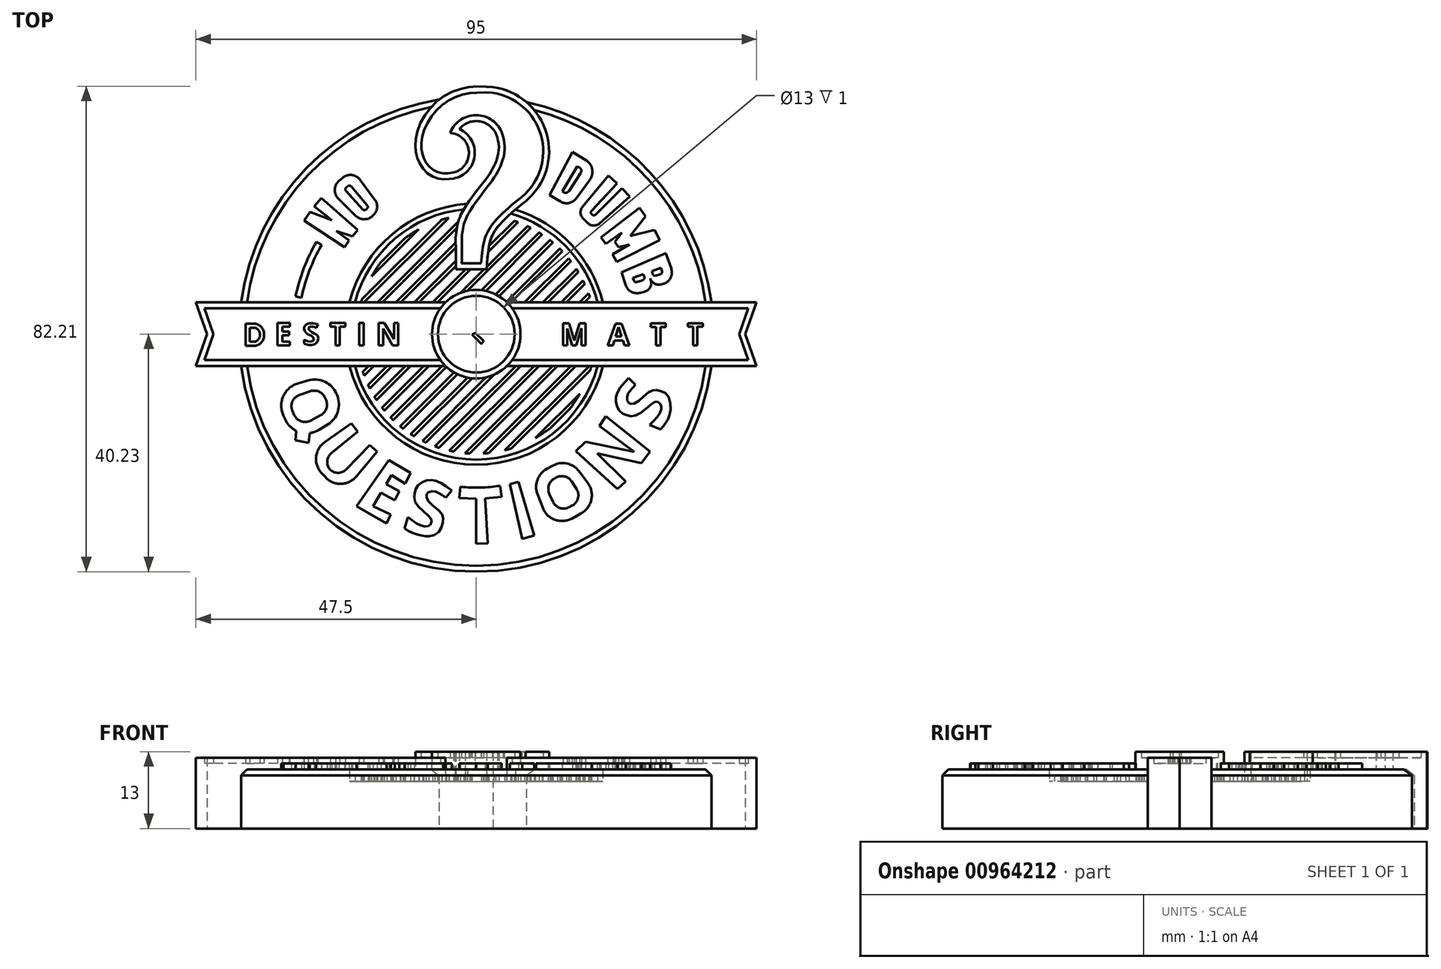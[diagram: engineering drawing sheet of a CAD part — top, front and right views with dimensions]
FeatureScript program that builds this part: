
annotation { "Feature Type Name" : "Feature", "Feature Type Description" : "" }
export const myFeature = defineFeature(function(context is Context, id is Id, definition is map)
    precondition{}
    {
        {
            var Q0;
            Q0=qCreatedBy(makeId("Top.planeOp"),FACE);
            var sketch = newSketch(context, id + "F0", { "sketchPlane" : qUnion([Q0])});
            skCircle(sketch, "E0", {"center": v(0, 0) * mm, "radius": 22.12 * mm});
            skCircle(sketch, "E1", {"center": v(0, 0) * mm, "radius": 40.23 * mm});
            skSolve(sketch);
        }
        {
            var Q0;
            Q0=qCreatedBy(makeId("Top.planeOp"),FACE);
            var sketch = newSketch(context, id + "F1", { "sketchPlane" : qUnion([Q0])});
            skCircle(sketch, "E2", {"center": v(0, 0) * mm, "radius": 22.25 * mm});
            skCircle(sketch, "E3.0", {"center": v(0, 0) * mm, "radius": 21.25 * mm});
            skCircle(sketch, "E4.0", {"center": v(0, 0) * mm, "radius": 20.25 * mm});
            skLineSegment(sketch, "E5", {"start": v(-14.52, -14.12) * mm, "end": v(14.16, 14.48) * mm});
            skLineSegment(sketch, "E6", {"start": v(-14.08, -14.55) * mm, "end": v(14.58, 14.05) * mm});
            skLineSegment(sketch, "E7.0.1.0", {"start": v(-15.97, -12.45) * mm, "end": v(12.5, 15.93) * mm});
            skLineSegment(sketch, "E7.0.2.0", {"start": v(-17.24, -10.62) * mm, "end": v(10.67, 17.21) * mm});
            skLineSegment(sketch, "E7.0.2.1", {"start": v(-16.9, -11.15) * mm, "end": v(11.18, 16.88) * mm});
            skLineSegment(sketch, "E7.1.7.0", {"start": v(-9.13, -18.07) * mm, "end": v(18.1, 9.08) * mm});
            skLineSegment(sketch, "E7.1.7.1", {"start": v(-8.54, -18.36) * mm, "end": v(18.37, 8.51) * mm});
            skLineSegment(sketch, "E7.1.8.0", {"start": v(-11.1, -16.93) * mm, "end": v(16.97, 11.05) * mm});
            skLineSegment(sketch, "E7.1.8.1", {"start": v(-10.57, -17.27) * mm, "end": v(17.3, 10.54) * mm});
            skLineSegment(sketch, "E7.1.9.0", {"start": v(-12.9, -15.61) * mm, "end": v(15.65, 12.85) * mm});
            skLineSegment(sketch, "E7.1.9.1", {"start": v(-12.4, -16) * mm, "end": v(16.02, 12.38) * mm});
            skLineSegment(sketch, "E8.trimOffspring", {"start": v(12.76, -15.72) * mm, "end": v(15.7, -12.8) * mm});
            skLineSegment(sketch, "E9.trimOffspring", {"start": v(10.02, -17.6) * mm, "end": v(17.57, -10.07) * mm});
            skLineSegment(sketch, "E10.trimOffspring", {"start": v(6.04, -19.33) * mm, "end": v(19.32, -6.07) * mm});
            skLineSegment(sketch, "E11.trimOffspring", {"start": v(4.83, -19.67) * mm, "end": v(19.65, -4.89) * mm});
            skLineSegment(sketch, "E12.trimOffspring", {"start": v(2.11, -20.14) * mm, "end": v(20.14, -2.15) * mm});
            skLineSegment(sketch, "E13.trimOffspring", {"start": v(1.16, -20.22) * mm, "end": v(20.21, -1.22) * mm});
            skLineSegment(sketch, "E14.trimOffspring", {"start": v(-1.9, -20.16) * mm, "end": v(20.17, 1.84) * mm});
            skLineSegment(sketch, "E15.trimOffspring", {"start": v(-1.08, -20.22) * mm, "end": v(20.22, 1.05) * mm});
            skLineSegment(sketch, "E16.trimOffspring", {"start": v(-3.85, -19.88) * mm, "end": v(19.89, 3.82) * mm});
            skLineSegment(sketch, "E17.trimOffspring", {"start": v(-4.58, -19.73) * mm, "end": v(19.74, 4.52) * mm});
            skLineSegment(sketch, "E18.trimOffspring", {"start": v(-6.32, -19.24) * mm, "end": v(19.25, 6.3) * mm});
            skLineSegment(sketch, "E19.trimOffspring", {"start": v(-6.98, -19.01) * mm, "end": v(19.03, 6.92) * mm});
            skLineSegment(sketch, "E20.trimOffspring", {"start": v(-15.58, -12.94) * mm, "end": v(12.97, 15.55) * mm});
            skLineSegment(sketch, "E21.trimOffspring", {"start": v(-18.05, -9.19) * mm, "end": v(9.22, 18.03) * mm});
            skLineSegment(sketch, "E22.trimOffspring", {"start": v(-18.33, -8.6) * mm, "end": v(8.66, 18.3) * mm});
            skLineSegment(sketch, "E23.trimOffspring", {"start": v(-19, -7.03) * mm, "end": v(7.06, 18.98) * mm});
            skLineSegment(sketch, "E24.trimOffspring", {"start": v(-19.22, -6.38) * mm, "end": v(6.44, 19.2) * mm});
            skLineSegment(sketch, "E25.trimOffspring", {"start": v(-19.71, -4.63) * mm, "end": v(4.7, 19.7) * mm});
            skLineSegment(sketch, "E26.trimOffspring", {"start": v(-19.87, -3.92) * mm, "end": v(3.98, 19.86) * mm});
            skLineSegment(sketch, "E27.trimOffspring", {"start": v(-20.15, -1.97) * mm, "end": v(2, 20.15) * mm});
            skLineSegment(sketch, "E28.trimOffspring", {"start": v(-20.22, -1.16) * mm, "end": v(1.22, 20.21) * mm});
            skLineSegment(sketch, "E29.trimOffspring", {"start": v(-20.22, 1.07) * mm, "end": v(-1.04, 20.22) * mm});
            skLineSegment(sketch, "E30.trimOffspring", {"start": v(-20.15, 2.01) * mm, "end": v(-1.95, 20.16) * mm});
            skLineSegment(sketch, "E31.trimOffspring", {"start": v(-19.7, 4.7) * mm, "end": v(-4.67, 19.7) * mm});
            skLineSegment(sketch, "E32.trimOffspring", {"start": v(-19.37, 5.9) * mm, "end": v(-5.83, 19.4) * mm});
            skLineSegment(sketch, "E33.trimOffspring", {"start": v(-17.74, 9.76) * mm, "end": v(-9.73, 17.76) * mm});
            skLineSegment(sketch, "E34.trimOffspring", {"start": v(-16.17, 12.2) * mm, "end": v(-12.15, 16.2) * mm});
            skSolve(sketch);
        }
        {
            var Q0;
            Q0=qCreatedBy(makeId("Top.planeOp"),FACE);
            cPlane(context, id + "F2", {"entities" : qUnion([Q0]), "cplaneType" : CPlaneType.OFFSET, "offset" : 10 * mm, "width" : 150 * mm, "height" : 150 * mm});
        }
        {
            var Q0;
            Q0=qCreatedBy(id+"F2.planeOp",FACE);
            var sketch = newSketch(context, id + "F3", { "sketchPlane" : qUnion([Q0])});
            skPoint(sketch, "E35.middle", {"position": v(0, 0) * mm});
            skArc(sketch, "E36", {"start": v(-17.48, 25.92) * mm, "mid": v(-14.44, 27.73) * mm, "end": v(-11.2, 29.19) * mm});
            skArc(sketch, "E37", {"start": v(-16.88, 25.03) * mm, "mid": v(-13.94, 26.78) * mm, "end": v(-10.82, 28.18) * mm});
            skLineSegment(sketch, "E38", {"start": v(0, 0) * mm, "end": v(-12.02, 31.32) * mm, "construction": true});
            skLineSegment(sketch, "E39", {"start": v(0, 0) * mm, "end": v(-17.92, 26.56) * mm, "construction": true});
            skLineSegment(sketch, "E40", {"start": v(0, 0) * mm, "end": v(-28.9, 16.69) * mm, "construction": true});
            skLineSegment(sketch, "E41", {"start": v(0, 0) * mm, "end": v(-31.67, 6.62) * mm, "construction": true});
            skArc(sketch, "E42", {"start": v(-26.19, 15.12) * mm, "mid": v(-28.25, 10.79) * mm, "end": v(-29.6, 6.18) * mm});
            skLineSegment(sketch, "E43", {"start": v(0, 0) * mm, "end": v(-36.69, 24.25) * mm, "construction": true});
            skLineSegment(sketch, "E44", {"start": v(0, 0) * mm, "end": v(-35.15, 25.88) * mm, "construction": true});
            skLineSegment(sketch, "E45", {"start": v(0, 0) * mm, "end": v(-34.07, 26.87) * mm, "construction": true});
            skLineSegment(sketch, "E46", {"start": v(0, 0) * mm, "end": v(-32.8, 28.77) * mm, "construction": true});
            skLineSegment(sketch, "E47", {"start": v(0, 0) * mm, "end": v(-26.52, 35.2) * mm, "construction": true});
            skLineSegment(sketch, "E48", {"start": v(-26.19, 15.12) * mm, "end": v(-27.08, 15.64) * mm});
            skLineSegment(sketch, "E49", {"start": v(-29.6, 6.18) * mm, "end": v(-30.61, 6.4) * mm});
            skLineSegment(sketch, "E50", {"start": v(-16.88, 25.03) * mm, "end": v(-17.48, 25.92) * mm});
            skLineSegment(sketch, "E51", {"start": v(-10.82, 28.18) * mm, "end": v(-11.2, 29.19) * mm});
            skArc(sketch, "E52", {"start": v(-26.73, 0) * mm, "mid": v(0, 26.73) * mm, "end": v(26.73, 0) * mm, "construction": true});
            skArc(sketch, "E53", {"start": v(-34.93, 0) * mm, "mid": v(0, 34.93) * mm, "end": v(34.93, 0) * mm, "construction": true});
            skLineSegment(sketch, "E54", {"start": v(0, 0) * mm, "end": v(-31.72, 31.17) * mm, "construction": true});
            skLineSegment(sketch, "E55", {"start": v(-22.3, 14.74) * mm, "end": v(-29.14, 19.26) * mm});
            skLineSegment(sketch, "E56", {"start": v(-21.52, 15.85) * mm, "end": v(-28.13, 20.71) * mm});
            skLineSegment(sketch, "E57", {"start": v(-20.98, 16.55) * mm, "end": v(-27.43, 21.64) * mm});
            skLineSegment(sketch, "E58", {"start": v(-20.1, 17.62) * mm, "end": v(-26.26, 23.04) * mm});
            skLineSegment(sketch, "E59", {"start": v(-28.13, 20.71) * mm, "end": v(-20.1, 17.62) * mm, "construction": true});
            skLineSegment(sketch, "E60", {"start": v(-20.98, 16.55) * mm, "end": v(-29.14, 19.26) * mm, "construction": true});
            skLineSegment(sketch, "E61", {"start": v(-19.73, 26.18) * mm, "end": v(-17.2, 22.83) * mm});
            skLineSegment(sketch, "E62", {"start": v(-23.38, 22.98) * mm, "end": v(-20.39, 20.03) * mm});
            skLineSegment(sketch, "E63", {"start": v(-23.3, 25.9) * mm, "end": v(-22.64, 26.48) * mm});
            skLineSegment(sketch, "E64", {"start": v(-17.67, 19.96) * mm, "end": v(-17.48, 20.12) * mm});
            skPoint(sketch, "E65.visualSharp", {"position": v(-21.02, 27.9) * mm});
            skArc(sketch, "E65.filletArc", {"start": v(-19.73, 26.18) * mm, "mid": v(-21.12, 26.97) * mm, "end": v(-22.64, 26.48) * mm});
            skPoint(sketch, "E66.visualSharp", {"position": v(-24.92, 24.49) * mm});
            skArc(sketch, "E66.filletArc", {"start": v(-23.3, 25.9) * mm, "mid": v(-23.98, 24.46) * mm, "end": v(-23.38, 22.98) * mm});
            skPoint(sketch, "E67.visualSharp", {"position": v(-16.08, 21.34) * mm});
            skArc(sketch, "E67.filletArc", {"start": v(-17.48, 20.12) * mm, "mid": v(-16.8, 21.42) * mm, "end": v(-17.2, 22.83) * mm});
            skPoint(sketch, "E68.visualSharp", {"position": v(-19.06, 18.73) * mm});
            skArc(sketch, "E68.filletArc", {"start": v(-20.39, 20.03) * mm, "mid": v(-19.04, 19.46) * mm, "end": v(-17.67, 19.96) * mm});
            skLineSegment(sketch, "E69", {"start": v(-20.98, 16.55) * mm, "end": v(-23.72, 17.46) * mm, "construction": true});
            skLineSegment(sketch, "E70", {"start": v(-20.98, 16.55) * mm, "end": v(-23.72, 17.46) * mm});
            skLineSegment(sketch, "E71", {"start": v(-28.13, 20.71) * mm, "end": v(-24.47, 19.3) * mm});
            skLineSegment(sketch, "E72", {"start": v(-29.14, 19.26) * mm, "end": v(-28.13, 20.71) * mm});
            skLineSegment(sketch, "E73", {"start": v(-27.43, 21.64) * mm, "end": v(-26.26, 23.04) * mm});
            skLineSegment(sketch, "E74", {"start": v(-20.98, 16.55) * mm, "end": v(-20.1, 17.62) * mm});
            skLineSegment(sketch, "E75", {"start": v(-22.3, 14.74) * mm, "end": v(-21.52, 15.85) * mm});
            skLineSegment(sketch, "E76", {"start": v(0, 0) * mm, "end": v(-29.4, 32.26) * mm, "construction": true});
            skLineSegment(sketch, "E77", {"start": v(0, 0) * mm, "end": v(-27.98, 33.07) * mm, "construction": true});
            skArc(sketch, "E78", {"start": v(28.2, 0) * mm, "mid": v(0, 28.2) * mm, "end": v(-28.2, 0) * mm, "construction": true});
            skArc(sketch, "E79", {"start": v(33.2, 0) * mm, "mid": v(0, 33.2) * mm, "end": v(-33.2, 0) * mm, "construction": true});
            skArc(sketch, "E80", {"start": v(30.07, 0) * mm, "mid": v(21.26, 21.26) * mm, "end": v(0, 30.07) * mm, "construction": true});
            skArc(sketch, "E81", {"start": v(31.59, 0) * mm, "mid": v(22.34, 22.34) * mm, "end": v(0, 31.59) * mm, "construction": true});
            skLineSegment(sketch, "E82", {"start": v(-19.26, 21.14) * mm, "end": v(-22.08, 24.23) * mm});
            skLineSegment(sketch, "E83", {"start": v(-22.04, 24.8) * mm, "end": v(-21.74, 25.07) * mm});
            skLineSegment(sketch, "E84", {"start": v(-21.17, 25.02) * mm, "end": v(-18.47, 21.83) * mm});
            skLineSegment(sketch, "E85", {"start": v(-18.51, 21.27) * mm, "end": v(-18.7, 21.1) * mm});
            skPoint(sketch, "E86.visualSharp", {"position": v(-22.36, 24.54) * mm});
            skArc(sketch, "E86.filletArc", {"start": v(-22.04, 24.8) * mm, "mid": v(-22.18, 24.53) * mm, "end": v(-22.08, 24.23) * mm});
            skPoint(sketch, "E87.visualSharp", {"position": v(-21.43, 25.33) * mm});
            skArc(sketch, "E87.filletArc", {"start": v(-21.17, 25.02) * mm, "mid": v(-21.45, 25.16) * mm, "end": v(-21.74, 25.07) * mm});
            skPoint(sketch, "E88.visualSharp", {"position": v(-18.22, 21.53) * mm});
            skArc(sketch, "E88.filletArc", {"start": v(-18.51, 21.27) * mm, "mid": v(-18.38, 21.54) * mm, "end": v(-18.47, 21.83) * mm});
            skPoint(sketch, "E89.visualSharp", {"position": v(-19, 20.85) * mm});
            skArc(sketch, "E89.filletArc", {"start": v(-19.26, 21.14) * mm, "mid": v(-18.98, 21) * mm, "end": v(-18.7, 21.1) * mm});
            skArc(sketch, "E90", {"start": v(-30.61, 6.4) * mm, "mid": v(-29.22, 11.16) * mm, "end": v(-27.08, 15.64) * mm});
            skLineSegment(sketch, "E91", {"start": v(0, 0) * mm, "end": v(19.18, 36.3) * mm, "construction": true});
            skLineSegment(sketch, "E92", {"start": v(0, 0) * mm, "end": v(21.24, 35.29) * mm, "construction": true});
            skLineSegment(sketch, "E93", {"start": v(0, 0) * mm, "end": v(22.48, 34.7) * mm, "construction": true});
            skLineSegment(sketch, "E94", {"start": v(0, 0) * mm, "end": v(24.33, 33.05) * mm, "construction": true});
            skLineSegment(sketch, "E95", {"start": v(0, 0) * mm, "end": v(26.82, 32.17) * mm, "construction": true});
            skLineSegment(sketch, "E96", {"start": v(0, 0) * mm, "end": v(28.64, 30.65) * mm, "construction": true});
            skLineSegment(sketch, "E97", {"start": v(0, 0) * mm, "end": v(30.98, 27.8) * mm, "construction": true});
            skLineSegment(sketch, "E98", {"start": v(0, 0) * mm, "end": v(29.35, 29.4) * mm, "construction": true});
            skLineSegment(sketch, "E99", {"start": v(0, 0) * mm, "end": v(32.72, 25.34) * mm, "construction": true});
            skLineSegment(sketch, "E100", {"start": v(0, 0) * mm, "end": v(38.58, 19.83) * mm, "construction": true});
            skLineSegment(sketch, "E101", {"start": v(0, 0) * mm, "end": v(39.4, 16.78) * mm, "construction": true});
            skLineSegment(sketch, "E102", {"start": v(0, 0) * mm, "end": v(40.92, 14.67) * mm, "construction": true});
            skLineSegment(sketch, "E103", {"start": v(0, 0) * mm, "end": v(41.16, 13.39) * mm, "construction": true});
            skLineSegment(sketch, "E104", {"start": v(0, 0) * mm, "end": v(42.33, 11.4) * mm, "construction": true});
            skLineSegment(sketch, "E105", {"start": v(0, 0) * mm, "end": v(41.86, 10.57) * mm, "construction": true});
            skLineSegment(sketch, "E106", {"start": v(0, 0) * mm, "end": v(34.36, 23.93) * mm, "construction": true});
            skLineSegment(sketch, "E107", {"start": v(0, 0) * mm, "end": v(37.3, 21.82) * mm, "construction": true});
            skLineSegment(sketch, "E108", {"start": v(0, 0) * mm, "end": v(35.65, 22.76) * mm, "construction": true});
            skLineSegment(sketch, "E109", {"start": v(0, 0) * mm, "end": v(34.66, 23.09) * mm, "construction": true});
            skLineSegment(sketch, "E110.MirrorCS", {"start": v(0, 0) * mm, "end": v(35.53, 21.73) * mm, "construction": true});
            skLineSegment(sketch, "E111", {"start": v(16.32, 30.89) * mm, "end": v(18.6, 29.46) * mm});
            skLineSegment(sketch, "E112", {"start": v(19.23, 26.12) * mm, "end": v(16.93, 23) * mm});
            skLineSegment(sketch, "E113", {"start": v(14.28, 22.46) * mm, "end": v(12.45, 23.57) * mm});
            skLineSegment(sketch, "E114", {"start": v(12.45, 23.57) * mm, "end": v(16.32, 30.89) * mm});
            skLineSegment(sketch, "E115", {"start": v(17.12, 28.44) * mm, "end": v(17.5, 28.22) * mm});
            skLineSegment(sketch, "E116", {"start": v(17.7, 27.32) * mm, "end": v(15.71, 24.25) * mm});
            skLineSegment(sketch, "E117", {"start": v(14.75, 24.05) * mm, "end": v(14.55, 24.17) * mm});
            skLineSegment(sketch, "E118", {"start": v(14.55, 24.17) * mm, "end": v(17.12, 28.44) * mm});
            skPoint(sketch, "E119.visualSharp", {"position": v(20.71, 28.13) * mm});
            skArc(sketch, "E119.filletArc", {"start": v(19.23, 26.12) * mm, "mid": v(19.64, 27.93) * mm, "end": v(18.6, 29.46) * mm});
            skPoint(sketch, "E120.visualSharp", {"position": v(15.85, 21.52) * mm});
            skArc(sketch, "E120.filletArc", {"start": v(14.28, 22.46) * mm, "mid": v(15.7, 22.21) * mm, "end": v(16.93, 23) * mm});
            skPoint(sketch, "E121.visualSharp", {"position": v(18.06, 27.88) * mm});
            skArc(sketch, "E121.filletArc", {"start": v(17.7, 27.32) * mm, "mid": v(17.79, 27.82) * mm, "end": v(17.5, 28.22) * mm});
            skPoint(sketch, "E122.visualSharp", {"position": v(15.33, 23.67) * mm});
            skArc(sketch, "E122.filletArc", {"start": v(14.75, 24.05) * mm, "mid": v(15.27, 23.95) * mm, "end": v(15.71, 24.25) * mm});
            skLineSegment(sketch, "E123", {"start": v(23.85, 25.52) * mm, "end": v(22.4, 26.88) * mm});
            skLineSegment(sketch, "E124", {"start": v(22.4, 26.88) * mm, "end": v(18, 21.6) * mm});
            skLineSegment(sketch, "E125", {"start": v(18.12, 19.56) * mm, "end": v(18.89, 18.82) * mm});
            skLineSegment(sketch, "E126", {"start": v(20.93, 18.78) * mm, "end": v(26, 23.33) * mm});
            skLineSegment(sketch, "E127", {"start": v(26, 23.33) * mm, "end": v(24.68, 24.72) * mm});
            skLineSegment(sketch, "E128", {"start": v(24.68, 24.72) * mm, "end": v(20.2, 20.24) * mm});
            skLineSegment(sketch, "E129", {"start": v(19.64, 20.24) * mm, "end": v(19.54, 20.34) * mm});
            skLineSegment(sketch, "E130", {"start": v(19.53, 20.9) * mm, "end": v(23.85, 25.52) * mm});
            skPoint(sketch, "E131.visualSharp", {"position": v(19.9, 17.85) * mm});
            skArc(sketch, "E131.filletArc", {"start": v(18.89, 18.82) * mm, "mid": v(19.9, 18.4) * mm, "end": v(20.93, 18.78) * mm});
            skPoint(sketch, "E132.visualSharp", {"position": v(17.11, 20.53) * mm});
            skArc(sketch, "E132.filletArc", {"start": v(18, 21.6) * mm, "mid": v(17.66, 20.56) * mm, "end": v(18.12, 19.56) * mm});
            skPoint(sketch, "E133.visualSharp", {"position": v(19.26, 20.62) * mm});
            skArc(sketch, "E133.filletArc", {"start": v(19.53, 20.9) * mm, "mid": v(19.42, 20.62) * mm, "end": v(19.54, 20.34) * mm});
            skPoint(sketch, "E134.visualSharp", {"position": v(19.92, 19.96) * mm});
            skArc(sketch, "E134.filletArc", {"start": v(19.64, 20.24) * mm, "mid": v(19.92, 20.12) * mm, "end": v(20.2, 20.24) * mm});
            skArc(sketch, "E135", {"start": v(30.94, 0) * mm, "mid": v(21.88, 21.88) * mm, "end": v(0, 30.94) * mm, "construction": true});
            skLineSegment(sketch, "E136", {"start": v(24.59, 10.47) * mm, "end": v(25.32, 8.3) * mm});
            skLineSegment(sketch, "E137", {"start": v(27.7, 7) * mm, "end": v(28.52, 7.2) * mm});
            skLineSegment(sketch, "E138", {"start": v(31.32, 8.43) * mm, "end": v(31.66, 8.52) * mm});
            skLineSegment(sketch, "E139", {"start": v(33.03, 11.1) * mm, "end": v(32.14, 13.7) * mm});
            skLineSegment(sketch, "E140", {"start": v(32.14, 13.7) * mm, "end": v(24.59, 10.47) * mm});
            skLineSegment(sketch, "E141", {"start": v(0, 0) * mm, "end": v(41.39, 12.16) * mm, "construction": true});
            skLineSegment(sketch, "E142", {"start": v(29.69, 8.72) * mm, "end": v(29.6, 9.05) * mm});
            skPoint(sketch, "E143.visualSharp", {"position": v(25.91, 6.54) * mm});
            skArc(sketch, "E143.filletArc", {"start": v(25.32, 8.3) * mm, "mid": v(26.26, 7.18) * mm, "end": v(27.7, 7) * mm});
            skPoint(sketch, "E144.visualSharp", {"position": v(30, 7.58) * mm});
            skArc(sketch, "E144.filletArc", {"start": v(28.52, 7.2) * mm, "mid": v(29.45, 7.9) * mm, "end": v(29.6, 9.05) * mm});
            skPoint(sketch, "E145.visualSharp", {"position": v(33.73, 9.08) * mm});
            skArc(sketch, "E145.filletArc", {"start": v(31.66, 8.52) * mm, "mid": v(32.9, 9.52) * mm, "end": v(33.03, 11.1) * mm});
            skLineSegment(sketch, "E146", {"start": v(29.48, 9.48) * mm, "end": v(29.69, 8.72) * mm});
            skPoint(sketch, "E147.visualSharp", {"position": v(29.87, 8.04) * mm});
            skArc(sketch, "E147.filletArc", {"start": v(29.48, 9.48) * mm, "mid": v(30.18, 8.58) * mm, "end": v(31.32, 8.43) * mm});
            skLineSegment(sketch, "E148", {"start": v(26.55, 9.52) * mm, "end": v(26.7, 9.1) * mm});
            skLineSegment(sketch, "E149", {"start": v(27.2, 8.84) * mm, "end": v(28.21, 9.18) * mm});
            skLineSegment(sketch, "E150", {"start": v(28.47, 9.68) * mm, "end": v(28.32, 10.15) * mm});
            skLineSegment(sketch, "E151", {"start": v(28.32, 10.15) * mm, "end": v(26.55, 9.52) * mm});
            skLineSegment(sketch, "E152", {"start": v(29.73, 10.66) * mm, "end": v(29.91, 10.14) * mm});
            skLineSegment(sketch, "E153", {"start": v(30.41, 9.9) * mm, "end": v(31.2, 10.14) * mm});
            skLineSegment(sketch, "E154", {"start": v(31.45, 10.65) * mm, "end": v(31.27, 11.21) * mm});
            skLineSegment(sketch, "E155", {"start": v(31.27, 11.21) * mm, "end": v(29.73, 10.66) * mm});
            skPoint(sketch, "E156.visualSharp", {"position": v(26.82, 8.72) * mm});
            skArc(sketch, "E156.filletArc", {"start": v(26.7, 9.1) * mm, "mid": v(26.89, 8.87) * mm, "end": v(27.2, 8.84) * mm});
            skPoint(sketch, "E157.visualSharp", {"position": v(28.6, 9.3) * mm});
            skArc(sketch, "E157.filletArc", {"start": v(28.21, 9.18) * mm, "mid": v(28.45, 9.37) * mm, "end": v(28.47, 9.68) * mm});
            skPoint(sketch, "E158.visualSharp", {"position": v(30.04, 9.77) * mm});
            skArc(sketch, "E158.filletArc", {"start": v(29.91, 10.14) * mm, "mid": v(30.11, 9.91) * mm, "end": v(30.41, 9.9) * mm});
            skPoint(sketch, "E159.visualSharp", {"position": v(31.57, 10.27) * mm});
            skArc(sketch, "E159.filletArc", {"start": v(31.2, 10.14) * mm, "mid": v(31.42, 10.34) * mm, "end": v(31.45, 10.65) * mm});
            skLineSegment(sketch, "E160", {"start": v(21.13, 16.36) * mm, "end": v(21.93, 15.28) * mm});
            skLineSegment(sketch, "E161", {"start": v(21.93, 15.28) * mm, "end": v(24.67, 17.19) * mm});
            skLineSegment(sketch, "E162", {"start": v(24.67, 17.19) * mm, "end": v(23.47, 15.63) * mm});
            skLineSegment(sketch, "E163", {"start": v(23.47, 15.63) * mm, "end": v(24.08, 14.72) * mm});
            skLineSegment(sketch, "E164", {"start": v(24.08, 14.72) * mm, "end": v(25.95, 15.19) * mm});
            skLineSegment(sketch, "E165", {"start": v(25.95, 15.19) * mm, "end": v(23.07, 13.5) * mm});
            skLineSegment(sketch, "E166", {"start": v(23.07, 13.5) * mm, "end": v(23.8, 12.24) * mm});
            skLineSegment(sketch, "E167", {"start": v(23.8, 12.24) * mm, "end": v(31.07, 15.97) * mm});
            skLineSegment(sketch, "E168", {"start": v(31.07, 15.97) * mm, "end": v(30.2, 17.67) * mm});
            skLineSegment(sketch, "E169", {"start": v(30.2, 17.67) * mm, "end": v(26.08, 16.65) * mm});
            skLineSegment(sketch, "E170", {"start": v(26.08, 16.65) * mm, "end": v(28.67, 19.97) * mm});
            skLineSegment(sketch, "E171", {"start": v(28.67, 19.97) * mm, "end": v(27.66, 21.42) * mm});
            skLineSegment(sketch, "E172", {"start": v(27.66, 21.42) * mm, "end": v(21.13, 16.36) * mm});
            skSolve(sketch);
        }
        {
            var Q0;
            Q0=qCreatedBy(id+"F2.planeOp",FACE);
            var sketch = newSketch(context, id + "F4", { "sketchPlane" : qUnion([Q0])});
            skArc(sketch, "E173", {"start": v(-26, 0) * mm, "mid": v(0, -26) * mm, "end": v(26, 0) * mm, "construction": true});
            skArc(sketch, "E174", {"start": v(-35.5, 0) * mm, "mid": v(0, -35.5) * mm, "end": v(35.5, 0) * mm, "construction": true});
            skLineSegment(sketch, "E175", {"start": v(0, 0) * mm, "end": v(-42.38, -11.68) * mm, "construction": true});
            skLineSegment(sketch, "E176", {"start": v(0, 0) * mm, "end": v(-42.12, -14.5) * mm, "construction": true});
            skLineSegment(sketch, "E177", {"start": v(0, 0) * mm, "end": v(-39.57, -20.63) * mm, "construction": true});
            skLineSegment(sketch, "E178", {"start": v(0, 0) * mm, "end": v(-38.55, -23.44) * mm, "construction": true});
            skLineSegment(sketch, "E179", {"start": v(0, 0) * mm, "end": v(-37.55, -24.34) * mm, "construction": true});
            skLineSegment(sketch, "E180", {"start": v(0, 0) * mm, "end": v(-36.48, -25.99) * mm, "construction": true});
            skLineSegment(sketch, "E181", {"start": v(0, 0) * mm, "end": v(-34.37, -28.21) * mm, "construction": true});
            skLineSegment(sketch, "E182", {"start": v(0, 0) * mm, "end": v(-30.39, -31.61) * mm, "construction": true});
            skLineSegment(sketch, "E183", {"start": v(0, 0) * mm, "end": v(-28.05, -33.25) * mm, "construction": true});
            skLineSegment(sketch, "E184", {"start": v(0, 0) * mm, "end": v(-24.41, -35.13) * mm, "construction": true});
            skLineSegment(sketch, "E185", {"start": v(0, 0) * mm, "end": v(-22.3, -37.12) * mm, "construction": true});
            skLineSegment(sketch, "E186", {"start": v(0, 0) * mm, "end": v(-18.67, -39.35) * mm, "construction": true});
            skLineSegment(sketch, "E187", {"start": v(0, 0) * mm, "end": v(-15.5, -40.87) * mm, "construction": true});
            skLineSegment(sketch, "E188", {"start": v(0, 0) * mm, "end": v(-12.8, -41.46) * mm, "construction": true});
            skLineSegment(sketch, "E189", {"start": v(0, 0) * mm, "end": v(-10.11, -42.04) * mm, "construction": true});
            skLineSegment(sketch, "E190", {"start": v(0, 0) * mm, "end": v(-7.42, -42.4) * mm, "construction": true});
            skLineSegment(sketch, "E191", {"start": v(0, 0) * mm, "end": v(-4.37, -42.4) * mm, "construction": true});
            skLineSegment(sketch, "E192", {"start": v(0, 0) * mm, "end": v(2.31, -42.28) * mm, "construction": true});
            skLineSegment(sketch, "E193", {"start": v(0, 0) * mm, "end": v(6.53, -41.7) * mm, "construction": true});
            skLineSegment(sketch, "E194", {"start": v(0, 0) * mm, "end": v(9.34, -41.7) * mm, "construction": true});
            skLineSegment(sketch, "E195", {"start": v(0, 0) * mm, "end": v(11.8, -41.1) * mm, "construction": true});
            skLineSegment(sketch, "E196", {"start": v(0, 0) * mm, "end": v(15.56, -40.64) * mm, "construction": true});
            skLineSegment(sketch, "E197", {"start": v(0, 0) * mm, "end": v(18.13, -39.58) * mm, "construction": true});
            skLineSegment(sketch, "E198", {"start": v(0, 0) * mm, "end": v(23.33, -36) * mm, "construction": true});
            skLineSegment(sketch, "E199", {"start": v(0, 0) * mm, "end": v(26.13, -34.86) * mm, "construction": true});
            skLineSegment(sketch, "E200", {"start": v(0, 0) * mm, "end": v(29.84, -32.78) * mm, "construction": true});
            skLineSegment(sketch, "E201", {"start": v(0, 0) * mm, "end": v(32.46, -31.96) * mm, "construction": true});
            skLineSegment(sketch, "E202", {"start": v(0, 0) * mm, "end": v(34.9, -26) * mm, "construction": true});
            skLineSegment(sketch, "E203", {"start": v(0, 0) * mm, "end": v(35.43, -23.91) * mm, "construction": true});
            skLineSegment(sketch, "E204", {"start": v(0, 0) * mm, "end": v(30.96, -29.01) * mm, "construction": true});
            skLineSegment(sketch, "E205", {"start": v(0, 0) * mm, "end": v(33.65, -26.3) * mm, "construction": true});
            skLineSegment(sketch, "E206", {"start": v(0, 0) * mm, "end": v(39.04, -20.72) * mm, "construction": true});
            skLineSegment(sketch, "E207", {"start": v(0, 0) * mm, "end": v(40.59, -18.27) * mm, "construction": true});
            skLineSegment(sketch, "E208", {"start": v(0, 0) * mm, "end": v(41.17, -15.7) * mm, "construction": true});
            skLineSegment(sketch, "E209", {"start": v(0, 0) * mm, "end": v(42.04, -12.99) * mm, "construction": true});
            skArc(sketch, "E210", {"start": v(-27.88, 0) * mm, "mid": v(0, -27.88) * mm, "end": v(27.88, 0) * mm, "construction": true});
            skArc(sketch, "E211", {"start": v(-33.84, 0) * mm, "mid": v(0, -33.84) * mm, "end": v(33.84, 0) * mm, "construction": true});
            skArc(sketch, "E212", {"start": v(-33.37, 0) * mm, "mid": v(0, -33.37) * mm, "end": v(33.37, 0) * mm, "construction": true});
            skArc(sketch, "E213", {"start": v(-31.33, 0) * mm, "mid": v(0, -31.33) * mm, "end": v(31.33, 0) * mm, "construction": true});
            skArc(sketch, "E214", {"start": v(-29.65, 0) * mm, "mid": v(0, -29.65) * mm, "end": v(29.65, 0) * mm, "construction": true});
            skArc(sketch, "E215", {"start": v(-35, 0) * mm, "mid": v(0, -35) * mm, "end": v(35, 0) * mm, "construction": true});
            skArc(sketch, "E216", {"start": v(-26.65, 0) * mm, "mid": v(0, -26.65) * mm, "end": v(26.65, 0) * mm, "construction": true});
            skArc(sketch, "E217", {"start": v(-34.6, 0) * mm, "mid": v(-24.47, -24.47) * mm, "end": v(0, -34.6) * mm, "construction": true});
            skArc(sketch, "E218", {"start": v(-32.7, 0) * mm, "mid": v(-23.13, -23.13) * mm, "end": v(0, -32.7) * mm, "construction": true});
            skLineSegment(sketch, "E219", {"start": v(0, 0) * mm, "end": v(-38.79, -22.77) * mm, "construction": true});
            skLineSegment(sketch, "E220", {"start": v(0, 0) * mm, "end": v(-39.38, -21.72) * mm, "construction": true});
            skLineSegment(sketch, "E221", {"start": v(0, 0) * mm, "end": v(-41.75, -17.7) * mm, "construction": true});
            skLineSegment(sketch, "E222", {"start": v(-28.4, -18.4) * mm, "end": v(-28.2, -16.56) * mm});
            skLineSegment(sketch, "E223", {"start": v(-28.4, -18.4) * mm, "end": v(-30.61, -17.97) * mm});
            skLineSegment(sketch, "E224", {"start": v(-32.68, -13.86) * mm, "end": v(-32.3, -14.62) * mm});
            skLineSegment(sketch, "E225", {"start": v(-26.66, -16.2) * mm, "end": v(-25.19, -15.32) * mm});
            skLineSegment(sketch, "E226", {"start": v(-23.6, -10.31) * mm, "end": v(-23.69, -10.1) * mm});
            skLineSegment(sketch, "E227", {"start": v(-28.42, -7.83) * mm, "end": v(-30.1, -8.3) * mm});
            skLineSegment(sketch, "E228", {"start": v(-32.82, -13.47) * mm, "end": v(-32.68, -13.86) * mm});
            skPoint(sketch, "E229.visualSharp", {"position": v(-25.07, -6.9) * mm});
            skArc(sketch, "E229.filletArc", {"start": v(-23.69, -10.1) * mm, "mid": v(-25.63, -8.08) * mm, "end": v(-28.42, -7.83) * mm});
            skPoint(sketch, "E230.visualSharp", {"position": v(-22.22, -13.5) * mm});
            skArc(sketch, "E230.filletArc", {"start": v(-25.19, -15.32) * mm, "mid": v(-23.46, -13.11) * mm, "end": v(-23.6, -10.31) * mm});
            skPoint(sketch, "E231.visualSharp", {"position": v(-30.33, -18.44) * mm});
            skArc(sketch, "E231.filletArc", {"start": v(-32.3, -14.62) * mm, "mid": v(-29.82, -16.64) * mm, "end": v(-26.66, -16.2) * mm});
            skPoint(sketch, "E232.visualSharp", {"position": v(-34.22, -9.43) * mm});
            skArc(sketch, "E232.filletArc", {"start": v(-30.1, -8.3) * mm, "mid": v(-32.58, -10.3) * mm, "end": v(-32.82, -13.47) * mm});
            skLineSegment(sketch, "E233", {"start": v(-30.61, -17.97) * mm, "end": v(-30.48, -16.39) * mm});
            skPoint(sketch, "E234.visualSharp", {"position": v(-27.58, -4.06) * mm});
            skLineSegment(sketch, "E235", {"start": v(-21.18, -15.08) * mm, "end": v(-25.68, -18.3) * mm});
            skLineSegment(sketch, "E236", {"start": v(-26.22, -23.52) * mm, "end": v(-25.58, -24.22) * mm});
            skLineSegment(sketch, "E237", {"start": v(-20.33, -24.1) * mm, "end": v(-16.76, -19.88) * mm});
            skLineSegment(sketch, "E238", {"start": v(-16.76, -19.88) * mm, "end": v(-18.06, -18.78) * mm});
            skLineSegment(sketch, "E239", {"start": v(-18.06, -18.78) * mm, "end": v(-21.98, -22.86) * mm});
            skLineSegment(sketch, "E240", {"start": v(-24.71, -23.03) * mm, "end": v(-24.89, -22.84) * mm});
            skLineSegment(sketch, "E241", {"start": v(-24.51, -20.12) * mm, "end": v(-20.1, -16.5) * mm});
            skLineSegment(sketch, "E242", {"start": v(-20.1, -16.5) * mm, "end": v(-21.18, -15.08) * mm});
            skPoint(sketch, "E243.visualSharp", {"position": v(-28.91, -20.6) * mm});
            skArc(sketch, "E243.filletArc", {"start": v(-25.68, -18.3) * mm, "mid": v(-27.13, -20.78) * mm, "end": v(-26.22, -23.52) * mm});
            skPoint(sketch, "E244.visualSharp", {"position": v(-22.89, -27.14) * mm});
            skArc(sketch, "E244.filletArc", {"start": v(-25.58, -24.22) * mm, "mid": v(-22.93, -25.35) * mm, "end": v(-20.33, -24.1) * mm});
            skPoint(sketch, "E245.visualSharp", {"position": v(-23.45, -24.4) * mm});
            skArc(sketch, "E245.filletArc", {"start": v(-24.89, -22.84) * mm, "mid": v(-23.44, -23.48) * mm, "end": v(-21.98, -22.86) * mm});
            skPoint(sketch, "E246.visualSharp", {"position": v(-26.15, -21.47) * mm});
            skArc(sketch, "E246.filletArc", {"start": v(-24.51, -20.12) * mm, "mid": v(-25.24, -21.53) * mm, "end": v(-24.71, -23.03) * mm});
            skLineSegment(sketch, "E247", {"start": v(-28.12, -9.67) * mm, "end": v(-29.96, -10.3) * mm});
            skLineSegment(sketch, "E248", {"start": v(-31.15, -12.99) * mm, "end": v(-30.86, -13.66) * mm});
            skLineSegment(sketch, "E249", {"start": v(-28.1, -14.64) * mm, "end": v(-26.37, -13.74) * mm});
            skLineSegment(sketch, "E250", {"start": v(-25.45, -11.18) * mm, "end": v(-25.63, -10.77) * mm});
            skPoint(sketch, "E251.visualSharp", {"position": v(-32, -11) * mm});
            skArc(sketch, "E251.filletArc", {"start": v(-29.96, -10.3) * mm, "mid": v(-31.14, -11.39) * mm, "end": v(-31.15, -12.99) * mm});
            skPoint(sketch, "E252.visualSharp", {"position": v(-30, -15.64) * mm});
            skArc(sketch, "E252.filletArc", {"start": v(-30.86, -13.66) * mm, "mid": v(-29.69, -14.76) * mm, "end": v(-28.1, -14.64) * mm});
            skPoint(sketch, "E253.visualSharp", {"position": v(-24.72, -12.89) * mm});
            skArc(sketch, "E253.filletArc", {"start": v(-26.37, -13.74) * mm, "mid": v(-25.4, -12.64) * mm, "end": v(-25.45, -11.18) * mm});
            skPoint(sketch, "E254.visualSharp", {"position": v(-26.36, -9.07) * mm});
            skArc(sketch, "E254.filletArc", {"start": v(-25.63, -10.77) * mm, "mid": v(-26.66, -9.73) * mm, "end": v(-28.12, -9.67) * mm});
            skLineSegment(sketch, "E255", {"start": v(-11.14, -23.5) * mm, "end": v(-14.84, -21.35) * mm});
            skLineSegment(sketch, "E256", {"start": v(-14.84, -21.35) * mm, "end": v(-20.26, -29.15) * mm});
            skLineSegment(sketch, "E257", {"start": v(-20.26, -29.15) * mm, "end": v(-15.22, -32.07) * mm});
            skLineSegment(sketch, "E258", {"start": v(-15.22, -32.07) * mm, "end": v(-14.5, -30.57) * mm});
            skLineSegment(sketch, "E259", {"start": v(-14.5, -30.57) * mm, "end": v(-17.5, -29.14) * mm});
            skLineSegment(sketch, "E260", {"start": v(-15.27, -25.42) * mm, "end": v(-14.36, -23.9) * mm});
            skLineSegment(sketch, "E261", {"start": v(-14.36, -23.9) * mm, "end": v(-12, -25.3) * mm});
            skLineSegment(sketch, "E262", {"start": v(-12, -25.3) * mm, "end": v(-11.14, -23.5) * mm});
            skLineSegment(sketch, "E263", {"start": v(0, 0) * mm, "end": v(-19.16, -39.14) * mm, "construction": true});
            skLineSegment(sketch, "E264", {"start": v(-17.5, -29.14) * mm, "end": v(-16.13, -26.85) * mm});
            skLineSegment(sketch, "E265", {"start": v(-16.13, -26.85) * mm, "end": v(-13.77, -28.13) * mm});
            skLineSegment(sketch, "E266", {"start": v(-13.77, -28.13) * mm, "end": v(-13.04, -26.63) * mm});
            skLineSegment(sketch, "E267", {"start": v(-13.04, -26.63) * mm, "end": v(-15.27, -25.42) * mm});
            skLineSegment(sketch, "E268", {"start": v(-2.67, -25.86) * mm, "end": v(-2.86, -27.73) * mm});
            skLineSegment(sketch, "E269", {"start": v(-2.86, -27.73) * mm, "end": v(0, -27.88) * mm});
            skLineSegment(sketch, "E270", {"start": v(0, -27.88) * mm, "end": v(0, -35.5) * mm});
            skLineSegment(sketch, "E271", {"start": v(0, -35.5) * mm, "end": v(1.94, -35.45) * mm});
            skLineSegment(sketch, "E272", {"start": v(1.94, -35.45) * mm, "end": v(1.52, -27.84) * mm});
            skLineSegment(sketch, "E273", {"start": v(1.52, -27.84) * mm, "end": v(4.31, -27.54) * mm});
            skLineSegment(sketch, "E274", {"start": v(4.31, -27.54) * mm, "end": v(4.02, -25.69) * mm});
            skLineSegment(sketch, "E275", {"start": v(5.69, -25.37) * mm, "end": v(7.76, -34.64) * mm});
            skLineSegment(sketch, "E276", {"start": v(7.76, -34.64) * mm, "end": v(9.8, -34.12) * mm});
            skLineSegment(sketch, "E277", {"start": v(9.8, -34.12) * mm, "end": v(7.18, -25) * mm});
            skLineSegment(sketch, "E278", {"start": v(7.18, -25) * mm, "end": v(5.69, -25.37) * mm});
            skArc(sketch, "E279", {"start": v(4.02, -25.69) * mm, "mid": v(0.68, -26) * mm, "end": v(-2.67, -25.86) * mm});
            skLineSegment(sketch, "E280", {"start": v(10.38, -27.13) * mm, "end": v(11.25, -29.4) * mm});
            skLineSegment(sketch, "E281", {"start": v(16.21, -31.2) * mm, "end": v(17.77, -30.35) * mm});
            skLineSegment(sketch, "E282", {"start": v(18.88, -25.18) * mm, "end": v(17.42, -23.24) * mm});
            skLineSegment(sketch, "E283", {"start": v(12.93, -22.27) * mm, "end": v(11.96, -22.81) * mm});
            skLineSegment(sketch, "E284", {"start": v(12.39, -27.04) * mm, "end": v(13, -28.38) * mm});
            skLineSegment(sketch, "E285", {"start": v(16.98, -26.2) * mm, "end": v(16.17, -24.95) * mm});
            skLineSegment(sketch, "E286", {"start": v(13.53, -24.29) * mm, "end": v(13.24, -24.45) * mm});
            skPoint(sketch, "E287.visualSharp", {"position": v(12.7, -33.15) * mm});
            skArc(sketch, "E287.filletArc", {"start": v(11.25, -29.4) * mm, "mid": v(13.32, -31.43) * mm, "end": v(16.21, -31.2) * mm});
            skPoint(sketch, "E288.visualSharp", {"position": v(21.3, -28.4) * mm});
            skArc(sketch, "E288.filletArc", {"start": v(17.77, -30.35) * mm, "mid": v(19.5, -28.02) * mm, "end": v(18.88, -25.18) * mm});
            skPoint(sketch, "E289.visualSharp", {"position": v(15.6, -20.8) * mm});
            skArc(sketch, "E289.filletArc", {"start": v(17.42, -23.24) * mm, "mid": v(15.36, -21.92) * mm, "end": v(12.93, -22.27) * mm});
            skPoint(sketch, "E290.visualSharp", {"position": v(9.3, -24.28) * mm});
            skArc(sketch, "E290.filletArc", {"start": v(11.96, -22.81) * mm, "mid": v(10.36, -24.67) * mm, "end": v(10.38, -27.13) * mm});
            skPoint(sketch, "E291.visualSharp", {"position": v(15.16, -23.4) * mm});
            skArc(sketch, "E291.filletArc", {"start": v(16.17, -24.95) * mm, "mid": v(14.98, -24.1) * mm, "end": v(13.53, -24.29) * mm});
            skPoint(sketch, "E292.visualSharp", {"position": v(11.61, -25.34) * mm});
            skArc(sketch, "E292.filletArc", {"start": v(13.24, -24.45) * mm, "mid": v(12.3, -25.57) * mm, "end": v(12.39, -27.04) * mm});
            skLineSegment(sketch, "E293", {"start": v(17.5, -19.23) * mm, "end": v(23.9, -26.25) * mm});
            skLineSegment(sketch, "E294", {"start": v(23.9, -26.25) * mm, "end": v(25.33, -24.95) * mm});
            skLineSegment(sketch, "E295", {"start": v(25.33, -24.95) * mm, "end": v(19.86, -19.56) * mm});
            skLineSegment(sketch, "E296", {"start": v(27.97, -21.86) * mm, "end": v(29.42, -19.86) * mm});
            skLineSegment(sketch, "E297", {"start": v(29.42, -19.86) * mm, "end": v(21.97, -13.9) * mm});
            skLineSegment(sketch, "E298", {"start": v(21.97, -13.9) * mm, "end": v(20.85, -15.53) * mm});
            skLineSegment(sketch, "E299", {"start": v(20.85, -15.53) * mm, "end": v(26.76, -19.93) * mm});
            skLineSegment(sketch, "E300", {"start": v(26.76, -19.93) * mm, "end": v(18.53, -18.24) * mm});
            skLineSegment(sketch, "E301", {"start": v(18.53, -18.24) * mm, "end": v(16.86, -19.8) * mm});
            skLineSegment(sketch, "E302", {"start": v(0, 0) * mm, "end": v(29, -34.05) * mm, "construction": true});
            skLineSegment(sketch, "E303", {"start": v(0, 0) * mm, "end": v(37.93, -24.02) * mm, "construction": true});
            skLineSegment(sketch, "E304", {"start": v(23.9, -26.25) * mm, "end": v(16.86, -19.8) * mm});
            skLineSegment(sketch, "E305", {"start": v(15.78, -29.3) * mm, "end": v(16.26, -29.04) * mm});
            skPoint(sketch, "E306.visualSharp", {"position": v(18.15, -28) * mm});
            skArc(sketch, "E306.filletArc", {"start": v(16.26, -29.04) * mm, "mid": v(17.24, -27.77) * mm, "end": v(16.98, -26.2) * mm});
            skPoint(sketch, "E307.visualSharp", {"position": v(13.9, -30.34) * mm});
            skArc(sketch, "E307.filletArc", {"start": v(13, -28.38) * mm, "mid": v(14.2, -29.45) * mm, "end": v(15.78, -29.3) * mm});
            skLineSegment(sketch, "E308", {"start": v(19.86, -19.56) * mm, "end": v(21.13, -20.8) * mm});
            skLineSegment(sketch, "E309", {"start": v(27.97, -21.86) * mm, "end": v(20.5, -20.18) * mm});
            skFitSpline(sketch, "E310", {"points": [v(-4.16, -26.46) * mm, v(-6.76, -24.88) * mm, v(-8.38, -24.8) * mm, v(-10, -25.75) * mm, v(-10.5, -27.12) * mm, v(-10.2, -28.65) * mm, v(-7.96, -30.93) * mm, v(-7.55, -31.71) * mm, v(-7.84, -32.33) * mm, v(-8.5, -32.59) * mm, v(-9.8, -32.24) * mm, v(-11.58, -30.98) * mm], "startDerivative": vector(-21.8, 15.36) * mm, "endDerivative": vector(-16.83, 13.47) * mm});
            skLineSegment(sketch, "E311", {"start": v(-11.58, -30.98) * mm, "end": v(-12.14, -32.89) * mm});
            skLineSegment(sketch, "E312", {"start": v(-4.16, -26.46) * mm, "end": v(-5.16, -27.7) * mm});
            skFitSpline(sketch, "E313", {"points": [v(-12.14, -32.89) * mm, v(-10.8, -33.69) * mm, v(-9.17, -34.13) * mm, v(-7.99, -34.26) * mm, v(-6.3, -33.43) * mm, v(-5.62, -31.61) * mm, v(-6, -30.24) * mm, v(-8.24, -28.1) * mm, v(-8.4, -27.2) * mm, v(-8.18, -26.8) * mm, v(-7.19, -26.6) * mm, v(-6.33, -26.91) * mm, v(-5.16, -27.7) * mm], "startDerivative": vector(14.29, -10.06) * mm, "endDerivative": vector(14.44, -10.42) * mm});
            skFitSpline(sketch, "E314", {"points": [v(25.83, -7.43) * mm, v(23.93, -9.82) * mm, v(23.65, -11.4) * mm, v(24.4, -13.13) * mm, v(25.7, -13.8) * mm, v(27.25, -13.7) * mm, v(29.79, -11.76) * mm, v(30.62, -11.45) * mm, v(31.2, -11.81) * mm, v(31.37, -12.5) * mm, v(30.86, -13.74) * mm, v(29.39, -15.35) * mm], "startDerivative": vector(-17.95, -19.73) * mm, "endDerivative": vector(-15.45, -15.03) * mm});
            skLineSegment(sketch, "E315", {"start": v(29.39, -15.35) * mm, "end": v(31.21, -16.15) * mm});
            skLineSegment(sketch, "E316", {"start": v(25.83, -7.43) * mm, "end": v(26.93, -8.57) * mm});
            skFitSpline(sketch, "E317", {"points": [v(31.21, -16.15) * mm, v(32.17, -14.92) * mm, v(32.82, -13.36) * mm, v(32.48, -10.42) * mm, v(30.76, -9.52) * mm, v(29.35, -9.73) * mm, v(26.94, -11.69) * mm, v(26.04, -11.73) * mm, v(25.6, -11.36) * mm, v(25.58, -10.45) * mm, v(26, -9.64) * mm, v(26.93, -8.57) * mm], "startDerivative": vector(11.75, 12.93) * mm, "endDerivative": vector(12.13, 13.03) * mm});
            skSolve(sketch);
        }
        {
            var Q0;
            Q0=qCreatedBy(makeId("Top.planeOp"),FACE);
            var sketch = newSketch(context, id + "F5", { "sketchPlane" : qUnion([Q0])});
            skLineSegment(sketch, "E318.bottom", {"start": v(47.5, -5.4) * mm, "end": v(-47.5, -5.4) * mm});
            skLineSegment(sketch, "E318.top", {"start": v(47.5, 5.4) * mm, "end": v(-47.5, 5.4) * mm});
            skLineSegment(sketch, "E319", {"start": v(45.59, 0) * mm, "end": v(47.5, -5.4) * mm});
            skLineSegment(sketch, "E320", {"start": v(45.59, 0) * mm, "end": v(47.5, 5.4) * mm});
            skLineSegment(sketch, "E321", {"start": v(-45.59, 0) * mm, "end": v(-47.5, 5.4) * mm});
            skLineSegment(sketch, "E322", {"start": v(-45.59, 0) * mm, "end": v(-47.5, -5.4) * mm});
            skLineSegment(sketch, "E323.0", {"start": v(44.53, 0) * mm, "end": v(46.09, -4.4) * mm});
            skLineSegment(sketch, "E323.1", {"start": v(46.09, -4.4) * mm, "end": v(-46.09, -4.4) * mm});
            skLineSegment(sketch, "E323.2", {"start": v(-44.53, 0) * mm, "end": v(-46.09, -4.4) * mm});
            skLineSegment(sketch, "E324.0", {"start": v(44.53, 0) * mm, "end": v(46.09, 4.4) * mm});
            skLineSegment(sketch, "E324.1", {"start": v(46.09, 4.4) * mm, "end": v(-46.09, 4.4) * mm});
            skLineSegment(sketch, "E324.2", {"start": v(-44.53, 0) * mm, "end": v(-46.09, 4.4) * mm});
            skSolve(sketch);
        }
        {
            var Q0;
            Q0=qCreatedBy(makeId("Top.planeOp"),FACE);
            var sketch = newSketch(context, id + "F6", { "sketchPlane" : qUnion([Q0])});
            skLineSegment(sketch, "E325", {"start": v(-2.47, 11.97) * mm, "end": v(0.8, 11.97) * mm});
            skPoint(sketch, "E326", {"position": v(-0.99, 21.02) * mm});
            skPoint(sketch, "E327", {"position": v(7.72, 23.27) * mm});
            skFitSpline(sketch, "E328", {"points": [v(-0.99, 21.02) * mm, v(-2.47, 11.97) * mm], "startDerivative": vector(-6.2, -10.24) * mm, "endDerivative": vector(-0.54, -10.85) * mm});
            skFitSpline(sketch, "E329", {"points": [v(7.72, 23.27) * mm, v(3.22, 19.19) * mm, v(1.4, 16) * mm, v(0.8, 11.97) * mm], "startDerivative": vector(-13.35, -10.58) * mm, "endDerivative": vector(-1.17, -13.33) * mm});
            skArc(sketch, "E330", {"start": v(-4.02, 27.36) * mm, "mid": v(-1.25, 30.9) * mm, "end": v(-4.4, 34.1) * mm});
            skArc(sketch, "E331", {"start": v(7.72, 23.27) * mm, "mid": v(10.95, 33.7) * mm, "end": v(2.71, 40.87) * mm});
            skFitSpline(sketch, "E332", {"points": [v(2.71, 40.87) * mm, v(-2.39, 40.55) * mm, v(-6.82, 37.85) * mm, v(-9.18, 33.34) * mm, v(-9.1, 30.4) * mm, v(-8.07, 28.49) * mm, v(-6.19, 27.36) * mm, v(-4.02, 27.36) * mm], "startDerivative": vector(-30.15, 2.21) * mm, "endDerivative": vector(14.25, 2.75) * mm});
            skArc(sketch, "E333", {"start": v(4.55, 33.47) * mm, "mid": v(0.31, 37.1) * mm, "end": v(-4.4, 34.1) * mm});
            skFitSpline(sketch, "E334", {"points": [v(4.55, 33.47) * mm, v(4.73, 30.53) * mm, v(3.67, 27.58) * mm, v(1.96, 25.06) * mm, v(-0.99, 21.02) * mm], "startDerivative": vector(3.23, -12.35) * mm, "endDerivative": vector(-9.9, -15.67) * mm});
            skCircle(sketch, "E335", {"center": v(0, 0) * mm, "radius": 7.5 * mm});
            skCircle(sketch, "E336.0", {"center": v(0, 0) * mm, "radius": 6.5 * mm});
            skFitSpline(sketch, "E337.0", {"points": [v(8.34, 22.49) * mm, v(7.8, 22.05) * mm, v(6.7, 21.17) * mm, v(5.23, 19.87) * mm, v(4, 18.62) * mm, v(3.12, 17.47) * mm, v(2.63, 16.52) * mm, v(2.34, 15.7) * mm, v(2.18, 15.03) * mm, v(2.05, 14.3) * mm, v(1.92, 13.27) * mm, v(1.85, 12.44) * mm, v(1.8, 11.89) * mm]});
            skLineSegment(sketch, "E337.1", {"start": v(-3.47, 10.97) * mm, "end": v(1.78, 10.97) * mm});
            skArc(sketch, "E337.2", {"start": v(8.35, 22.5) * mm, "mid": v(11.91, 33.99) * mm, "end": v(2.82, 41.86) * mm});
            skFitSpline(sketch, "E337.3", {"points": [v(-1.84, 21.54) * mm, v(-2.4, 20.63) * mm, v(-2.96, 19.36) * mm, v(-3.33, 17.77) * mm, v(-3.5, 16.25) * mm, v(-3.45, 14.44) * mm, v(-3.43, 12.89) * mm, v(-3.47, 12.02) * mm]});
            skFitSpline(sketch, "E337.4", {"points": [v(2.79, 41.86) * mm, v(2.14, 41.91) * mm, v(0.85, 41.98) * mm, v(-0.78, 41.89) * mm, v(-2.08, 41.67) * mm, v(-3.37, 41.33) * mm, v(-4.94, 40.66) * mm, v(-6.38, 39.68) * mm, v(-7.4, 38.72) * mm, v(-8.34, 37.64) * mm, v(-9.28, 36.14) * mm, v(-9.92, 34.59) * mm, v(-10.22, 33.37) * mm, v(-10.33, 32.5) * mm, v(-10.33, 31.66) * mm, v(-10.24, 30.88) * mm, v(-10.08, 30.15) * mm, v(-9.84, 29.47) * mm, v(-9.53, 28.81) * mm, v(-9.14, 28.2) * mm, v(-8.67, 27.65) * mm, v(-8.1, 27.15) * mm, v(-7.45, 26.74) * mm, v(-6.84, 26.49) * mm, v(-6.3, 26.35) * mm, v(-5.77, 26.27) * mm, v(-5.12, 26.24) * mm, v(-4.42, 26.28) * mm, v(-4.01, 26.34) * mm, v(-3.84, 26.37) * mm]});
            skArc(sketch, "E337.5", {"start": v(-3.84, 26.37) * mm, "mid": v(-0.27, 30.2) * mm, "end": v(-2.88, 34.74) * mm});
            skArc(sketch, "E337.6", {"start": v(3.58, 33.23) * mm, "mid": v(0.82, 36) * mm, "end": v(-2.88, 34.74) * mm});
            skFitSpline(sketch, "E337.7", {"points": [v(3.59, 33.22) * mm, v(3.7, 32.77) * mm, v(3.81, 32.08) * mm, v(3.8, 31.15) * mm, v(3.72, 30.47) * mm, v(3.53, 29.76) * mm, v(3.28, 29.05) * mm, v(2.96, 28.36) * mm, v(2.6, 27.71) * mm, v(2.22, 27.1) * mm, v(1.78, 26.48) * mm, v(1.3, 25.83) * mm, v(0.73, 25.11) * mm, v(0.12, 24.32) * mm, v(-0.74, 23.19) * mm, v(-1.4, 22.24) * mm, v(-1.83, 21.56) * mm]});
            skLineSegment(sketch, "E338", {"start": v(-3.47, 12.02) * mm, "end": v(-3.47, 10.97) * mm});
            skLineSegment(sketch, "E339", {"start": v(1.8, 11.89) * mm, "end": v(1.78, 10.97) * mm});
            skLineSegment(sketch, "E340", {"start": v(-1.83, 21.56) * mm, "end": v(-1.84, 21.54) * mm});
            skLineSegment(sketch, "E341", {"start": v(3.58, 33.23) * mm, "end": v(3.59, 33.22) * mm});
            skLineSegment(sketch, "E342", {"start": v(2.79, 41.86) * mm, "end": v(2.82, 41.86) * mm});
            skLineSegment(sketch, "E343", {"start": v(8.34, 22.49) * mm, "end": v(8.35, 22.5) * mm});
            skSolve(sketch);
        }
        {
            var Q0;
            Q0=qCreatedBy(makeId("Top.planeOp"),FACE);
            cPlane(context, id + "F7", {"entities" : qUnion([Q0]), "cplaneType" : CPlaneType.OFFSET, "offset" : 11 * mm, "width" : 150 * mm, "height" : 150 * mm});
        }
        {
            var Q0;
            Q0=qCreatedBy(id+"F7.planeOp",FACE);
            var sketch = newSketch(context, id + "F8", { "sketchPlane" : qUnion([Q0])});
            skLineSegment(sketch, "E344.bottom", {"start": v(-39.06, 1.8) * mm, "end": v(-37.74, 1.8) * mm});
            skLineSegment(sketch, "E344.top", {"start": v(-39.06, -2) * mm, "end": v(-37.74, -2) * mm});
            skLineSegment(sketch, "E344.left", {"start": v(-39.06, 1.8) * mm, "end": v(-39.06, -2) * mm});
            skLineSegment(sketch, "E344.right", {"start": v(-35.94, 0) * mm, "end": v(-35.94, -0.2) * mm});
            skPoint(sketch, "E345.visualSharp", {"position": v(-35.94, 1.8) * mm});
            skArc(sketch, "E345.filletArc", {"start": v(-35.94, 0) * mm, "mid": v(-36.47, 1.27) * mm, "end": v(-37.74, 1.8) * mm});
            skPoint(sketch, "E346.visualSharp", {"position": v(-35.94, -2) * mm});
            skArc(sketch, "E346.filletArc", {"start": v(-37.74, -2) * mm, "mid": v(-36.47, -1.46) * mm, "end": v(-35.94, -0.2) * mm});
            skLineSegment(sketch, "E347", {"start": v(-33.66, 1.9) * mm, "end": v(-33.66, -1.9) * mm});
            skPoint(sketch, "E347.endSnap0", {"position": v(-38.4, -2) * mm});
            skLineSegment(sketch, "E348", {"start": v(-33.66, -1.9) * mm, "end": v(-31.56, -1.9) * mm});
            skLineSegment(sketch, "E349", {"start": v(-31.56, -1.9) * mm, "end": v(-31.56, -1.26) * mm});
            skLineSegment(sketch, "E350", {"start": v(-31.56, -1.26) * mm, "end": v(-32.86, -1.26) * mm});
            skLineSegment(sketch, "E351", {"start": v(-32.86, -1.26) * mm, "end": v(-32.86, -0.2) * mm});
            skLineSegment(sketch, "E352", {"start": v(-32.86, -0.2) * mm, "end": v(-31.7, -0.2) * mm});
            skLineSegment(sketch, "E353", {"start": v(-31.7, -0.2) * mm, "end": v(-31.7, 0.44) * mm});
            skLineSegment(sketch, "E354", {"start": v(-31.7, 0.44) * mm, "end": v(-32.86, 0.44) * mm});
            skLineSegment(sketch, "E355", {"start": v(-32.86, 0.44) * mm, "end": v(-32.86, 1.27) * mm});
            skLineSegment(sketch, "E356", {"start": v(-32.86, 1.27) * mm, "end": v(-31.56, 1.27) * mm});
            skLineSegment(sketch, "E357", {"start": v(-31.56, 1.27) * mm, "end": v(-31.56, 1.9) * mm});
            skLineSegment(sketch, "E358", {"start": v(-31.56, 1.9) * mm, "end": v(-33.66, 1.9) * mm});
            skLineSegment(sketch, "E359.0", {"start": v(-38.36, 1.1) * mm, "end": v(-38.36, -1.3) * mm});
            skArc(sketch, "E359.1", {"start": v(-36.64, 0) * mm, "mid": v(-36.97, 0.78) * mm, "end": v(-37.74, 1.1) * mm});
            skLineSegment(sketch, "E359.2", {"start": v(-36.64, 0) * mm, "end": v(-36.64, -0.2) * mm});
            skLineSegment(sketch, "E359.3", {"start": v(-38.36, 1.1) * mm, "end": v(-37.74, 1.1) * mm});
            skArc(sketch, "E359.4", {"start": v(-37.74, -1.3) * mm, "mid": v(-36.97, -0.97) * mm, "end": v(-36.64, -0.2) * mm});
            skLineSegment(sketch, "E359.5", {"start": v(-38.36, -1.3) * mm, "end": v(-37.74, -1.3) * mm});
            skLineSegment(sketch, "E360", {"start": v(-51.1, 1.8) * mm, "end": v(49.4, 1.8) * mm, "construction": true});
            skLineSegment(sketch, "E361", {"start": v(-51.1, -2) * mm, "end": v(49.4, -1.9) * mm, "construction": true});
            skFitSpline(sketch, "E362", {"points": [v(-29.19, -0.94) * mm, v(-28.45, -1.2) * mm, v(-27.84, -1.2) * mm, v(-27.53, -0.93) * mm, v(-27.67, -0.48) * mm, v(-28.2, -0.17) * mm, v(-28.88, 0.28) * mm, v(-29.16, 0.93) * mm, v(-28.97, 1.5) * mm, v(-28.45, 1.8) * mm, v(-27.85, 1.85) * mm, v(-26.84, 1.66) * mm], "startDerivative": vector(6.84, -3.18) * mm, "endDerivative": vector(11.6, -2.74) * mm});
            skLineSegment(sketch, "E363", {"start": v(-26.84, 1.66) * mm, "end": v(-27.05, 1.08) * mm});
            skFitSpline(sketch, "E364", {"points": [v(-27.05, 1.08) * mm, v(-27.66, 1.27) * mm, v(-28.17, 1.26) * mm, v(-28.39, 1.02) * mm, v(-28.3, 0.74) * mm, v(-27.84, 0.34) * mm, v(-27.2, 0) * mm, v(-26.92, -0.24) * mm, v(-26.79, -0.67) * mm, v(-26.88, -1.21) * mm, v(-27.24, -1.6) * mm, v(-27.64, -1.8) * mm, v(-28.12, -1.85) * mm, v(-28.64, -1.79) * mm, v(-29.19, -1.61) * mm], "startDerivative": vector(-7.4, 2.87) * mm, "endDerivative": vector(-7.1, 2.63) * mm});
            skLineSegment(sketch, "E365", {"start": v(-29.19, -0.94) * mm, "end": v(-29.19, -1.61) * mm});
            skLineSegment(sketch, "E366", {"start": v(-24.75, 1.88) * mm, "end": v(-24.75, 1.27) * mm});
            skLineSegment(sketch, "E367", {"start": v(-24.75, 1.27) * mm, "end": v(-23.84, 1.27) * mm});
            skLineSegment(sketch, "E368", {"start": v(-23.84, 1.27) * mm, "end": v(-23.84, -1.89) * mm});
            skLineSegment(sketch, "E369", {"start": v(-23.84, -1.89) * mm, "end": v(-23.13, -1.89) * mm});
            skLineSegment(sketch, "E370", {"start": v(-23.13, -1.89) * mm, "end": v(-23.13, 1.27) * mm});
            skLineSegment(sketch, "E371", {"start": v(-23.13, 1.27) * mm, "end": v(-22.21, 1.27) * mm});
            skLineSegment(sketch, "E372", {"start": v(-22.21, 1.27) * mm, "end": v(-22.21, 1.88) * mm});
            skLineSegment(sketch, "E373", {"start": v(-22.21, 1.88) * mm, "end": v(-24.75, 1.88) * mm});
            skLineSegment(sketch, "E374.bottom", {"start": v(-19.81, 1.88) * mm, "end": v(-19.1, 1.88) * mm});
            skLineSegment(sketch, "E374.top", {"start": v(-19.81, -1.88) * mm, "end": v(-19.1, -1.88) * mm});
            skLineSegment(sketch, "E374.left", {"start": v(-19.81, 1.88) * mm, "end": v(-19.81, -1.88) * mm});
            skLineSegment(sketch, "E374.right", {"start": v(-19.1, 1.88) * mm, "end": v(-19.1, -1.88) * mm});
            skLineSegment(sketch, "E375.bottom", {"start": v(-16.5, 1.88) * mm, "end": v(-15.8, 1.88) * mm});
            skLineSegment(sketch, "E375.top", {"start": v(-16.5, -1.88) * mm, "end": v(-15.8, -1.88) * mm});
            skLineSegment(sketch, "E375.left", {"start": v(-16.5, 1.88) * mm, "end": v(-16.5, -1.88) * mm});
            skLineSegment(sketch, "E376.bottom", {"start": v(-13.94, 1.88) * mm, "end": v(-13.23, 1.88) * mm});
            skLineSegment(sketch, "E376.top", {"start": v(-13.94, -1.88) * mm, "end": v(-13.23, -1.88) * mm});
            skLineSegment(sketch, "E376.left", {"start": v(-13.94, 1.88) * mm, "end": v(-13.94, -0.84) * mm});
            skLineSegment(sketch, "E376.right", {"start": v(-13.23, 1.88) * mm, "end": v(-13.23, -1.88) * mm});
            skLineSegment(sketch, "E377", {"start": v(-15.57, 1.88) * mm, "end": v(-13.94, -0.84) * mm});
            skLineSegment(sketch, "E378", {"start": v(-15.8, 0.98) * mm, "end": v(-14.2, -1.88) * mm});
            skLineSegment(sketch, "E379", {"start": v(-14.2, -1.88) * mm, "end": v(-13.94, -1.88) * mm});
            skLineSegment(sketch, "E380", {"start": v(-15.57, 1.88) * mm, "end": v(-15.8, 1.88) * mm});
            skLineSegment(sketch, "E381.trimOffspring", {"start": v(-15.8, 0.98) * mm, "end": v(-15.8, -1.88) * mm});
            skLineSegment(sketch, "E382", {"start": v(29.57, 1.85) * mm, "end": v(29.57, 1.24) * mm});
            skLineSegment(sketch, "E383", {"start": v(29.57, 1.24) * mm, "end": v(30.48, 1.24) * mm});
            skLineSegment(sketch, "E384", {"start": v(30.48, 1.24) * mm, "end": v(30.48, -1.92) * mm});
            skLineSegment(sketch, "E385", {"start": v(30.48, -1.92) * mm, "end": v(31.2, -1.92) * mm});
            skLineSegment(sketch, "E386", {"start": v(31.2, -1.92) * mm, "end": v(31.2, 1.24) * mm});
            skLineSegment(sketch, "E387", {"start": v(31.2, 1.24) * mm, "end": v(32.1, 1.24) * mm});
            skLineSegment(sketch, "E388", {"start": v(32.1, 1.24) * mm, "end": v(32.1, 1.85) * mm});
            skLineSegment(sketch, "E389", {"start": v(32.1, 1.85) * mm, "end": v(29.57, 1.85) * mm});
            skLineSegment(sketch, "E390", {"start": v(35.83, 1.85) * mm, "end": v(35.83, 1.24) * mm});
            skLineSegment(sketch, "E391", {"start": v(35.83, 1.24) * mm, "end": v(36.74, 1.24) * mm});
            skLineSegment(sketch, "E392", {"start": v(36.74, 1.24) * mm, "end": v(36.74, -1.91) * mm});
            skLineSegment(sketch, "E393", {"start": v(36.74, -1.91) * mm, "end": v(37.45, -1.91) * mm});
            skLineSegment(sketch, "E394", {"start": v(37.45, -1.91) * mm, "end": v(37.45, 1.24) * mm});
            skLineSegment(sketch, "E395", {"start": v(37.45, 1.24) * mm, "end": v(38.37, 1.25) * mm});
            skLineSegment(sketch, "E396", {"start": v(38.37, 1.25) * mm, "end": v(38.37, 1.85) * mm});
            skLineSegment(sketch, "E397", {"start": v(38.37, 1.85) * mm, "end": v(35.83, 1.85) * mm});
            skLineSegment(sketch, "E398.bottom", {"start": v(14.69, 1.83) * mm, "end": v(15.4, 1.83) * mm});
            skLineSegment(sketch, "E398.top", {"start": v(14.69, -1.93) * mm, "end": v(15.4, -1.93) * mm});
            skLineSegment(sketch, "E398.left", {"start": v(14.69, 1.83) * mm, "end": v(14.69, -1.93) * mm});
            skLineSegment(sketch, "E398.right", {"start": v(15.4, 1.83) * mm, "end": v(15.4, 1.8) * mm});
            skLineSegment(sketch, "E399.bottom", {"start": v(17.8, 1.83) * mm, "end": v(18.52, 1.83) * mm});
            skLineSegment(sketch, "E399.top", {"start": v(17.8, -1.93) * mm, "end": v(18.52, -1.93) * mm});
            skLineSegment(sketch, "E399.right", {"start": v(18.52, 1.83) * mm, "end": v(18.52, -1.93) * mm});
            skLineSegment(sketch, "E400.left", {"start": v(24.62, -0.37) * mm, "end": v(23.62, -0.37) * mm});
            skLineSegment(sketch, "E400.right", {"start": v(24.85, -1.08) * mm, "end": v(23.4, -1.08) * mm});
            skLineSegment(sketch, "E401", {"start": v(22.3, -1.93) * mm, "end": v(23.63, 1.8) * mm});
            skLineSegment(sketch, "E402", {"start": v(23.13, -1.92) * mm, "end": v(23.4, -1.08) * mm});
            skLineSegment(sketch, "E403.MirrorCS", {"start": v(25.95, -1.92) * mm, "end": v(24.62, 1.8) * mm});
            skLineSegment(sketch, "E404.MirrorCS", {"start": v(25.11, -1.92) * mm, "end": v(24.85, -1.08) * mm});
            skLineSegment(sketch, "E405", {"start": v(23.63, 1.8) * mm, "end": v(24.62, 1.8) * mm});
            skLineSegment(sketch, "E406", {"start": v(22.3, -1.93) * mm, "end": v(23.13, -1.92) * mm});
            skLineSegment(sketch, "E407", {"start": v(25.11, -1.92) * mm, "end": v(25.95, -1.92) * mm});
            skLineSegment(sketch, "E408.trimOffspring", {"start": v(23.62, -0.37) * mm, "end": v(24.12, 1.2) * mm});
            skLineSegment(sketch, "E409.trimOffspring", {"start": v(24.62, -0.37) * mm, "end": v(24.12, 1.2) * mm});
            skLineSegment(sketch, "E410", {"start": v(15.4, 1.83) * mm, "end": v(15.72, 1.83) * mm});
            skLineSegment(sketch, "E411", {"start": v(15.72, 1.83) * mm, "end": v(16.6, -1.08) * mm});
            skLineSegment(sketch, "E412", {"start": v(16.25, -1.93) * mm, "end": v(15.4, 0.99) * mm});
            skLineSegment(sketch, "E413.MirrorCS", {"start": v(17.49, 1.83) * mm, "end": v(16.6, -1.08) * mm});
            skLineSegment(sketch, "E414.MirrorCS", {"start": v(16.97, -1.93) * mm, "end": v(17.8, 0.99) * mm});
            skLineSegment(sketch, "E415", {"start": v(16.25, -1.93) * mm, "end": v(16.97, -1.93) * mm});
            skLineSegment(sketch, "E416.trimOffspring", {"start": v(17.8, 0.99) * mm, "end": v(17.8, -1.93) * mm});
            skLineSegment(sketch, "E417", {"start": v(17.49, 1.83) * mm, "end": v(17.8, 1.83) * mm});
            skLineSegment(sketch, "E418.trimOffspring", {"start": v(15.4, 0.99) * mm, "end": v(15.4, -1.93) * mm});
            skLineSegment(sketch, "E419", {"start": v(-0.74, -0.08) * mm, "end": v(0.85, -1.63) * mm});
            skLineSegment(sketch, "E420", {"start": v(1.9, -2.65) * mm, "end": v(2.33, -2.21) * mm});
            skLineSegment(sketch, "E421", {"start": v(2.33, -2.21) * mm, "end": v(1.68, -1.59) * mm});
            skFitSpline(sketch, "E422", {"points": [v(0.85, -1.63) * mm, v(-0.1, -2.17) * mm, v(-0.9, -2.16) * mm, v(-1.5, -1.74) * mm, v(-1.57, -0.96) * mm, v(-0.74, -0.08) * mm], "startDerivative": vector(-3.96, -3.5) * mm, "endDerivative": vector(4.5, 3.58) * mm});
            skFitSpline(sketch, "E423", {"points": [v(0.85, -1.63) * mm, v(1.25, -1.17) * mm, v(1.8, -0.06) * mm], "startDerivative": vector(1.06, 0.87) * mm, "endDerivative": vector(0.42, 2.27) * mm});
            skLineSegment(sketch, "E424", {"start": v(1.8, -0.06) * mm, "end": v(2.5, -0.06) * mm});
            skFitSpline(sketch, "E425", {"points": [v(-0.74, -0.08) * mm, v(0.4, 0.6) * mm, v(0.95, 1.54) * mm, v(0.66, 2.45) * mm, v(0.16, 2.8) * mm, v(-0.9, 2.8) * mm, v(-1.51, 2.45) * mm, v(-1.78, 1.96) * mm, v(-1.8, 1.34) * mm, v(-1.49, 0.73) * mm, v(-1.14, 0.3) * mm], "startDerivative": vector(9.54, 4.63) * mm, "endDerivative": vector(4.16, -4.73) * mm});
            skLineSegment(sketch, "E426", {"start": v(-0.75, 0.82) * mm, "end": v(-0.56, 0.63) * mm});
            skLineSegment(sketch, "E427", {"start": v(-0.56, 0.63) * mm, "end": v(-0.41, 0.77) * mm});
            skFitSpline(sketch, "E428", {"points": [v(-0.41, 0.77) * mm, v(0.06, 1.18) * mm, v(0.25, 1.6) * mm, v(0.1, 2.05) * mm, v(-0.35, 2.32) * mm, v(-0.74, 2.28) * mm, v(-1.07, 2.03) * mm, v(-1.16, 1.61) * mm, v(-1.02, 1.2) * mm, v(-0.75, 0.82) * mm], "startDerivative": vector(4.08, 3.05) * mm, "endDerivative": vector(2.57, -3.3) * mm});
            skFitSpline(sketch, "E429", {"points": [v(-1.14, 0.3) * mm, v(-2.08, -0.45) * mm, v(-2.3, -1.35) * mm, v(-2.05, -2.24) * mm, v(-1.35, -2.69) * mm, v(-0.52, -2.78) * mm, v(0.28, -2.66) * mm, v(1.05, -2.27) * mm, v(1.3, -2.06) * mm, v(1.68, -1.59) * mm, v(2.5, -0.06) * mm], "startDerivative": vector(-9.37, -5.87) * mm, "endDerivative": vector(3.06, 14.04) * mm});
            skLineSegment(sketch, "E430.trimOffspring", {"start": v(1.25, -1.17) * mm, "end": v(-0.17, 0.2) * mm});
            skLineSegment(sketch, "E431.trimOffspring", {"start": v(1.3, -2.06) * mm, "end": v(1.9, -2.65) * mm});
            skFitSpline(sketch, "E432.trimOffspring", {"points": [v(-1.14, 0.3) * mm, v(-2.08, -0.45) * mm, v(-2.3, -1.35) * mm, v(-2.05, -2.24) * mm, v(-1.35, -2.69) * mm, v(-0.52, -2.78) * mm, v(0.28, -2.66) * mm, v(1.05, -2.27) * mm, v(1.3, -2.06) * mm, v(1.68, -1.59) * mm, v(2.5, -0.06) * mm], "startDerivative": vector(-9.37, -5.87) * mm, "endDerivative": vector(3.06, 14.04) * mm});
            skSolve(sketch);
        }
        {
            var Q0;
            Q0=makeQuery(id+"F0.imprint","IMPRINT",FACE,{"disambiguationData":[TD([[makeQuery(id+"F0.imprint","IMPRINT",EDGE,{"derivedFrom":sQuery(id+"F0.wireOp",EDGE,"E0")}),-1.0]])]});
            extrude(context, id + "F9", {"entities" : qUnion([Q0]), "depth" : 10 * mm, "offsetDistance" : 25 * mm});
        }
        {
            var Q0;
            Q0=makeQuery(id+"F9.opExtrude","CAP_EDGE",EDGE,{"disambiguationData":[OSD([sQuery(id+"F0.wireOp",EDGE,"E1")])],"isStart":false});
            chamfer(context, id + "F10", {"entities" : qUnion([Q0]), "width" : 1 * mm, "tangentPropagation" : true});
        }
        {
            var Q0;
            Q0=makeQuery(id+"F3.imprint","IMPRINT",FACE,{"disambiguationData":[TD([[makeQuery(id+"F3.imprint","IMPRINT",EDGE,{"derivedFrom":sQuery(id+"F3.wireOp",EDGE,"E55")}),-1.0]])]});
            var Q1;
            {var subQ2=sQuery(id+"F3.wireOp",EDGE,"E70");Q1=makeQuery(id+"F3.imprint","IMPRINT",FACE,{"disambiguationData":[TD([[makeQuery(id+"F3.imprint","IMPRINT",EDGE,{"derivedFrom":subQ2}),-1.0]])]});}
            var Q2;
            Q2=makeQuery(id+"F3.imprint","IMPRINT",FACE,{"disambiguationData":[TD([[makeQuery(id+"F3.imprint","IMPRINT",EDGE,{"derivedFrom":sQuery(id+"F3.wireOp",EDGE,"E58")}),1.0]])]});
            var Q3;
            Q3=makeQuery(id+"F3.imprint","IMPRINT",FACE,{"disambiguationData":[TD([[makeQuery(id+"F3.imprint","IMPRINT",EDGE,{"derivedFrom":sQuery(id+"F3.wireOp",EDGE,"E61")}),-1.0]])]});
            var Q4;
            Q4=makeQuery(id+"F3.imprint","IMPRINT",FACE,{"disambiguationData":[TD([[makeQuery(id+"F3.imprint","IMPRINT",EDGE,{"derivedFrom":sQuery(id+"F3.wireOp",EDGE,"E42")}),-1.0]])]});
            var Q5;
            Q5=makeQuery(id+"F3.imprint","IMPRINT",FACE,{"disambiguationData":[TD([[makeQuery(id+"F3.imprint","IMPRINT",EDGE,{"derivedFrom":sQuery(id+"F3.wireOp",EDGE,"E36")}),-1.0]])]});
            var Q6;
            Q6=makeQuery(id+"F3.imprint","IMPRINT",FACE,{"disambiguationData":[TD([[makeQuery(id+"F3.imprint","IMPRINT",EDGE,{"derivedFrom":sQuery(id+"F3.wireOp",EDGE,"E111")}),-1.0]])]});
            var Q7;
            Q7=makeQuery(id+"F3.imprint","IMPRINT",FACE,{"disambiguationData":[TD([[makeQuery(id+"F3.imprint","IMPRINT",EDGE,{"derivedFrom":sQuery(id+"F3.wireOp",EDGE,"E123")}),1.0]])]});
            var Q8;
            Q8=makeQuery(id+"F3.imprint","IMPRINT",FACE,{"disambiguationData":[TD([[makeQuery(id+"F3.imprint","IMPRINT",EDGE,{"derivedFrom":sQuery(id+"F3.wireOp",EDGE,"E160")}),1.0]])]});
            var Q9;
            Q9=makeQuery(id+"F3.imprint","IMPRINT",FACE,{"disambiguationData":[TD([[makeQuery(id+"F3.imprint","IMPRINT",EDGE,{"derivedFrom":sQuery(id+"F3.wireOp",EDGE,"E136")}),1.0]])]});
            extrude(context, id + "F11", {"entities" : qUnion([Q0, Q1, Q2, Q3, Q4, Q5, Q6, Q7, Q8, Q9]), "operationType" : NewBodyOperationType.ADD, "depth" : 1 * mm, "offsetDistance" : 25 * mm});
        }
        {
            var Q0;
            Q0=qSketchRegion(id+"F4",true);
            extrude(context, id + "F12", {"entities" : qUnion([Q0]), "operationType" : NewBodyOperationType.ADD, "depth" : 1 * mm, "offsetDistance" : 25 * mm});
        }
        {
            var Q0;
            Q0=qSketchRegion(id+"F5",true);
            var Q1;
            {var subQ0=sQuery(id+"F5.wireOp",EDGE,"E324.1");var subQ1=sQuery(id+"F5.wireOp",EDGE,"b35f8b2a-4b94-4131-818a-57236e89b0ba");var subQ2=makeQuery(id+"F5.imprint","INTERSECT",VERTEX,{"disambiguationData":[OD(1.0)],"derivedFrom":[subQ1,subQ0]});Q1=makeQuery(id+"F5.imprint","IMPRINT",FACE,{"disambiguationData":[TD([[makeQuery(id+"F5.imprint","IMPRINT",EDGE,{"disambiguationData":[TD([[subQ2,-1.0]])],"derivedFrom":subQ1}),1.0]])]});}
            var Q2;
            {var subQ0=sQuery(id+"F5.wireOp",EDGE,"E324.1");var subQ1=sQuery(id+"F5.wireOp",EDGE,"b35f8b2a-4b94-4131-818a-57236e89b0ba");var subQ2=makeQuery(id+"F5.imprint","INTERSECT",VERTEX,{"disambiguationData":[OD(0.0)],"derivedFrom":[subQ1,subQ0]});Q2=makeQuery(id+"F5.imprint","IMPRINT",FACE,{"disambiguationData":[TD([[makeQuery(id+"F5.imprint","IMPRINT",EDGE,{"disambiguationData":[TD([[subQ2,1.0]])],"derivedFrom":subQ1}),1.0]])]});}
            extrude(context, id + "F13", {"entities" : qUnion([Q0, Q1, Q2]), "operationType" : NewBodyOperationType.ADD, "depth" : 12 * mm, "offsetDistance" : 25 * mm});
        }
        {
            var Q0;
            {var subQ0=sQuery(id+"F1.wireOp",EDGE,"E34.trimOffspring");Q0=makeQuery(id+"F1.imprint","IMPRINT",FACE,{"disambiguationData":[TD([[makeQuery(id+"F1.imprint","IMPRINT",EDGE,{"derivedFrom":subQ0}),1.0]])]});}
            var Q1;
            Q1=makeQuery(id+"F1.imprint","IMPRINT",FACE,{"disambiguationData":[TD([[makeQuery(id+"F1.imprint","IMPRINT",EDGE,{"derivedFrom":sQuery(id+"F1.wireOp",EDGE,"E3.0")}),1.0]])]});
            var Q2;
            {var subQ0=sQuery(id+"F1.wireOp",EDGE,"E32.trimOffspring");Q2=makeQuery(id+"F1.imprint","IMPRINT",FACE,{"disambiguationData":[TD([[makeQuery(id+"F1.imprint","IMPRINT",EDGE,{"derivedFrom":subQ0}),1.0]])]});}
            var Q3;
            {var subQ0=sQuery(id+"F1.wireOp",EDGE,"E30.trimOffspring");Q3=makeQuery(id+"F1.imprint","IMPRINT",FACE,{"disambiguationData":[TD([[makeQuery(id+"F1.imprint","IMPRINT",EDGE,{"derivedFrom":subQ0}),1.0]])]});}
            var Q4;
            {var subQ0=sQuery(id+"F1.wireOp",EDGE,"E28.trimOffspring");Q4=makeQuery(id+"F1.imprint","IMPRINT",FACE,{"disambiguationData":[TD([[makeQuery(id+"F1.imprint","IMPRINT",EDGE,{"derivedFrom":subQ0}),1.0]])]});}
            var Q5;
            {var subQ0=sQuery(id+"F1.wireOp",EDGE,"E26.trimOffspring");Q5=makeQuery(id+"F1.imprint","IMPRINT",FACE,{"disambiguationData":[TD([[makeQuery(id+"F1.imprint","IMPRINT",EDGE,{"derivedFrom":subQ0}),1.0]])]});}
            var Q6;
            {var subQ0=sQuery(id+"F1.wireOp",EDGE,"E24.trimOffspring");Q6=makeQuery(id+"F1.imprint","IMPRINT",FACE,{"disambiguationData":[TD([[makeQuery(id+"F1.imprint","IMPRINT",EDGE,{"derivedFrom":subQ0}),1.0]])]});}
            var Q7;
            {var subQ0=sQuery(id+"F1.wireOp",EDGE,"E22.trimOffspring");Q7=makeQuery(id+"F1.imprint","IMPRINT",FACE,{"disambiguationData":[TD([[makeQuery(id+"F1.imprint","IMPRINT",EDGE,{"derivedFrom":subQ0}),1.0]])]});}
            var Q8;
            {var subQ0=sQuery(id+"F1.wireOp",EDGE,"E7.0.2.0");Q8=makeQuery(id+"F1.imprint","IMPRINT",FACE,{"disambiguationData":[TD([[makeQuery(id+"F1.imprint","IMPRINT",EDGE,{"derivedFrom":subQ0}),1.0]])]});}
            var Q9;
            {var subQ0=sQuery(id+"F1.wireOp",EDGE,"E7.0.1.0");Q9=makeQuery(id+"F1.imprint","IMPRINT",FACE,{"disambiguationData":[TD([[makeQuery(id+"F1.imprint","IMPRINT",EDGE,{"derivedFrom":subQ0}),1.0]])]});}
            var Q10;
            {var subQ0=sQuery(id+"F1.wireOp",EDGE,"E5");Q10=makeQuery(id+"F1.imprint","IMPRINT",FACE,{"disambiguationData":[TD([[makeQuery(id+"F1.imprint","IMPRINT",EDGE,{"derivedFrom":subQ0}),1.0]])]});}
            var Q11;
            {var subQ0=sQuery(id+"F1.wireOp",EDGE,"E6");Q11=makeQuery(id+"F1.imprint","IMPRINT",FACE,{"disambiguationData":[TD([[makeQuery(id+"F1.imprint","IMPRINT",EDGE,{"derivedFrom":subQ0}),-1.0]])]});}
            var Q12;
            {var subQ0=sQuery(id+"F1.wireOp",EDGE,"E7.1.8.0");Q12=makeQuery(id+"F1.imprint","IMPRINT",FACE,{"disambiguationData":[TD([[makeQuery(id+"F1.imprint","IMPRINT",EDGE,{"derivedFrom":subQ0}),1.0]])]});}
            var Q13;
            {var subQ0=sQuery(id+"F1.wireOp",EDGE,"E7.1.7.0");Q13=makeQuery(id+"F1.imprint","IMPRINT",FACE,{"disambiguationData":[TD([[makeQuery(id+"F1.imprint","IMPRINT",EDGE,{"derivedFrom":subQ0}),1.0]])]});}
            var Q14;
            {var subQ0=sQuery(id+"F1.wireOp",EDGE,"E7.1.7.1");Q14=makeQuery(id+"F1.imprint","IMPRINT",FACE,{"disambiguationData":[TD([[makeQuery(id+"F1.imprint","IMPRINT",EDGE,{"derivedFrom":subQ0}),-1.0]])]});}
            var Q15;
            {var subQ0=sQuery(id+"F1.wireOp",EDGE,"E17.trimOffspring");Q15=makeQuery(id+"F1.imprint","IMPRINT",FACE,{"disambiguationData":[TD([[makeQuery(id+"F1.imprint","IMPRINT",EDGE,{"derivedFrom":subQ0}),1.0]])]});}
            var Q16;
            {var subQ0=sQuery(id+"F1.wireOp",EDGE,"E14.trimOffspring");Q16=makeQuery(id+"F1.imprint","IMPRINT",FACE,{"disambiguationData":[TD([[makeQuery(id+"F1.imprint","IMPRINT",EDGE,{"derivedFrom":subQ0}),1.0]])]});}
            var Q17;
            {var subQ0=sQuery(id+"F1.wireOp",EDGE,"E13.trimOffspring");Q17=makeQuery(id+"F1.imprint","IMPRINT",FACE,{"disambiguationData":[TD([[makeQuery(id+"F1.imprint","IMPRINT",EDGE,{"derivedFrom":subQ0}),1.0]])]});}
            var Q18;
            {var subQ0=sQuery(id+"F1.wireOp",EDGE,"E11.trimOffspring");Q18=makeQuery(id+"F1.imprint","IMPRINT",FACE,{"disambiguationData":[TD([[makeQuery(id+"F1.imprint","IMPRINT",EDGE,{"derivedFrom":subQ0}),1.0]])]});}
            var Q19;
            {var subQ0=sQuery(id+"F1.wireOp",EDGE,"E9.trimOffspring");Q19=makeQuery(id+"F1.imprint","IMPRINT",FACE,{"disambiguationData":[TD([[makeQuery(id+"F1.imprint","IMPRINT",EDGE,{"derivedFrom":subQ0}),1.0]])]});}
            var Q20;
            {var subQ0=sQuery(id+"F1.wireOp",EDGE,"E8.trimOffspring");Q20=makeQuery(id+"F1.imprint","IMPRINT",FACE,{"disambiguationData":[TD([[makeQuery(id+"F1.imprint","IMPRINT",EDGE,{"derivedFrom":subQ0}),-1.0]])]});}
            extrude(context, id + "F14", {"entities" : qUnion([Q0, Q1, Q2, Q3, Q4, Q5, Q6, Q7, Q8, Q9, Q10, Q11, Q12, Q13, Q14, Q15, Q16, Q17, Q18, Q19, Q20]), "operationType" : NewBodyOperationType.ADD, "depth" : 9 * mm, "offsetDistance" : 25 * mm});
        }
        {
            var Q0;
            Q0=makeQuery(id+"F1.imprint","IMPRINT",FACE,{"disambiguationData":[TD([[makeQuery(id+"F1.imprint","IMPRINT",EDGE,{"derivedFrom":sQuery(id+"F1.wireOp",EDGE,"E2")}),1.0]])]});
            var Q1;
            {var subQ0=sQuery(id+"F1.wireOp",EDGE,"E33.trimOffspring");Q1=makeQuery(id+"F1.imprint","IMPRINT",FACE,{"disambiguationData":[TD([[makeQuery(id+"F1.imprint","IMPRINT",EDGE,{"derivedFrom":subQ0}),1.0]])]});}
            var Q2;
            {var subQ0=sQuery(id+"F1.wireOp",EDGE,"E31.trimOffspring");Q2=makeQuery(id+"F1.imprint","IMPRINT",FACE,{"disambiguationData":[TD([[makeQuery(id+"F1.imprint","IMPRINT",EDGE,{"derivedFrom":subQ0}),1.0]])]});}
            var Q3;
            {var subQ0=sQuery(id+"F1.wireOp",EDGE,"E29.trimOffspring");Q3=makeQuery(id+"F1.imprint","IMPRINT",FACE,{"disambiguationData":[TD([[makeQuery(id+"F1.imprint","IMPRINT",EDGE,{"derivedFrom":subQ0}),1.0]])]});}
            var Q4;
            {var subQ0=sQuery(id+"F1.wireOp",EDGE,"E27.trimOffspring");Q4=makeQuery(id+"F1.imprint","IMPRINT",FACE,{"disambiguationData":[TD([[makeQuery(id+"F1.imprint","IMPRINT",EDGE,{"derivedFrom":subQ0}),1.0]])]});}
            var Q5;
            {var subQ0=sQuery(id+"F1.wireOp",EDGE,"E25.trimOffspring");Q5=makeQuery(id+"F1.imprint","IMPRINT",FACE,{"disambiguationData":[TD([[makeQuery(id+"F1.imprint","IMPRINT",EDGE,{"derivedFrom":subQ0}),1.0]])]});}
            var Q6;
            {var subQ0=sQuery(id+"F1.wireOp",EDGE,"E23.trimOffspring");Q6=makeQuery(id+"F1.imprint","IMPRINT",FACE,{"disambiguationData":[TD([[makeQuery(id+"F1.imprint","IMPRINT",EDGE,{"derivedFrom":subQ0}),1.0]])]});}
            var Q7;
            {var subQ0=sQuery(id+"F1.wireOp",EDGE,"E21.trimOffspring");Q7=makeQuery(id+"F1.imprint","IMPRINT",FACE,{"disambiguationData":[TD([[makeQuery(id+"F1.imprint","IMPRINT",EDGE,{"derivedFrom":subQ0}),1.0]])]});}
            var Q8;
            {var subQ0=sQuery(id+"F1.wireOp",EDGE,"E7.0.2.0");Q8=makeQuery(id+"F1.imprint","IMPRINT",FACE,{"disambiguationData":[TD([[makeQuery(id+"F1.imprint","IMPRINT",EDGE,{"derivedFrom":subQ0}),-1.0]])]});}
            var Q9;
            {var subQ0=sQuery(id+"F1.wireOp",EDGE,"E7.0.1.0");Q9=makeQuery(id+"F1.imprint","IMPRINT",FACE,{"disambiguationData":[TD([[makeQuery(id+"F1.imprint","IMPRINT",EDGE,{"derivedFrom":subQ0}),-1.0]])]});}
            var Q10;
            {var subQ0=sQuery(id+"F1.wireOp",EDGE,"E5");Q10=makeQuery(id+"F1.imprint","IMPRINT",FACE,{"disambiguationData":[TD([[makeQuery(id+"F1.imprint","IMPRINT",EDGE,{"derivedFrom":subQ0}),-1.0]])]});}
            var Q11;
            {var subQ0=sQuery(id+"F1.wireOp",EDGE,"E7.1.9.0");Q11=makeQuery(id+"F1.imprint","IMPRINT",FACE,{"disambiguationData":[TD([[makeQuery(id+"F1.imprint","IMPRINT",EDGE,{"derivedFrom":subQ0}),-1.0]])]});}
            var Q12;
            {var subQ0=sQuery(id+"F1.wireOp",EDGE,"E7.1.8.0");Q12=makeQuery(id+"F1.imprint","IMPRINT",FACE,{"disambiguationData":[TD([[makeQuery(id+"F1.imprint","IMPRINT",EDGE,{"derivedFrom":subQ0}),-1.0]])]});}
            var Q13;
            {var subQ0=sQuery(id+"F1.wireOp",EDGE,"E7.1.7.0");Q13=makeQuery(id+"F1.imprint","IMPRINT",FACE,{"disambiguationData":[TD([[makeQuery(id+"F1.imprint","IMPRINT",EDGE,{"derivedFrom":subQ0}),-1.0]])]});}
            var Q14;
            {var subQ0=sQuery(id+"F1.wireOp",EDGE,"E18.trimOffspring");Q14=makeQuery(id+"F1.imprint","IMPRINT",FACE,{"disambiguationData":[TD([[makeQuery(id+"F1.imprint","IMPRINT",EDGE,{"derivedFrom":subQ0}),1.0]])]});}
            var Q15;
            {var subQ0=sQuery(id+"F1.wireOp",EDGE,"E16.trimOffspring");Q15=makeQuery(id+"F1.imprint","IMPRINT",FACE,{"disambiguationData":[TD([[makeQuery(id+"F1.imprint","IMPRINT",EDGE,{"derivedFrom":subQ0}),1.0]])]});}
            var Q16;
            {var subQ0=sQuery(id+"F1.wireOp",EDGE,"E14.trimOffspring");Q16=makeQuery(id+"F1.imprint","IMPRINT",FACE,{"disambiguationData":[TD([[makeQuery(id+"F1.imprint","IMPRINT",EDGE,{"derivedFrom":subQ0}),-1.0]])]});}
            var Q17;
            {var subQ0=sQuery(id+"F1.wireOp",EDGE,"E12.trimOffspring");Q17=makeQuery(id+"F1.imprint","IMPRINT",FACE,{"disambiguationData":[TD([[makeQuery(id+"F1.imprint","IMPRINT",EDGE,{"derivedFrom":subQ0}),1.0]])]});}
            var Q18;
            {var subQ0=sQuery(id+"F1.wireOp",EDGE,"E10.trimOffspring");Q18=makeQuery(id+"F1.imprint","IMPRINT",FACE,{"disambiguationData":[TD([[makeQuery(id+"F1.imprint","IMPRINT",EDGE,{"derivedFrom":subQ0}),1.0]])]});}
            var Q19;
            {var subQ0=sQuery(id+"F1.wireOp",EDGE,"E8.trimOffspring");Q19=makeQuery(id+"F1.imprint","IMPRINT",FACE,{"disambiguationData":[TD([[makeQuery(id+"F1.imprint","IMPRINT",EDGE,{"derivedFrom":subQ0}),1.0]])]});}
            extrude(context, id + "F15", {"entities" : qUnion([Q0, Q1, Q2, Q3, Q4, Q5, Q6, Q7, Q8, Q9, Q10, Q11, Q12, Q13, Q14, Q15, Q16, Q17, Q18, Q19]), "operationType" : NewBodyOperationType.ADD, "depth" : 8 * mm, "offsetDistance" : 25 * mm});
        }
        {
            var Q0;
            {var subQ4=sQuery(id+"F5.wireOp",EDGE,"E323.2");Q0=makeQuery(id+"F5.imprint","IMPRINT",FACE,{"disambiguationData":[TD([[makeQuery(id+"F5.imprint","IMPRINT",EDGE,{"derivedFrom":subQ4}),1.0]])]});}
            var Q1;
            {var subQ1=sQuery(id+"F5.wireOp",EDGE,"E323.0");Q1=makeQuery(id+"F5.imprint","IMPRINT",FACE,{"disambiguationData":[TD([[makeQuery(id+"F5.imprint","IMPRINT",EDGE,{"derivedFrom":subQ1}),-1.0]])]});}
            var Q2;
            {var subQ0=sQuery(id+"F5.wireOp",EDGE,"deff8420-59c7-402e-b318-feb89fa43c7f.0");var subQ1=sQuery(id+"F5.wireOp",EDGE,"E318.top");var subQ2=makeQuery(id+"F5.imprint","INTERSECT",VERTEX,{"disambiguationData":[OD(0.0)],"derivedFrom":[subQ1,subQ0]});Q2=makeQuery(id+"F5.imprint","IMPRINT",FACE,{"disambiguationData":[TD([[makeQuery(id+"F5.imprint","IMPRINT",EDGE,{"disambiguationData":[TD([[subQ2,-1.0]])],"derivedFrom":subQ1}),-1.0]])]});}
            var Q3;
            {var subQ0=sQuery(id+"F5.wireOp",EDGE,"deff8420-59c7-402e-b318-feb89fa43c7f.0");var subQ1=sQuery(id+"F5.wireOp",EDGE,"E318.top");var subQ2=makeQuery(id+"F5.imprint","INTERSECT",VERTEX,{"disambiguationData":[OD(0.0)],"derivedFrom":[subQ1,subQ0]});Q3=makeQuery(id+"F5.imprint","IMPRINT",FACE,{"disambiguationData":[TD([[makeQuery(id+"F5.imprint","IMPRINT",EDGE,{"disambiguationData":[TD([[subQ2,-1.0]])],"derivedFrom":subQ1}),1.0]])]});}
            var Q4;
            {var subQ0=sQuery(id+"F5.wireOp",EDGE,"E324.1");var subQ1=sQuery(id+"F5.wireOp",EDGE,"deff8420-59c7-402e-b318-feb89fa43c7f.0");var subQ2=makeQuery(id+"F5.imprint","INTERSECT",VERTEX,{"disambiguationData":[OD(1.0)],"derivedFrom":[subQ1,subQ0]});Q4=makeQuery(id+"F5.imprint","IMPRINT",FACE,{"disambiguationData":[TD([[makeQuery(id+"F5.imprint","IMPRINT",EDGE,{"disambiguationData":[TD([[subQ2,-1.0]])],"derivedFrom":subQ1}),1.0]])]});}
            var Q5;
            {var subQ0=sQuery(id+"F5.wireOp",EDGE,"deff8420-59c7-402e-b318-feb89fa43c7f.0");var subQ1=sQuery(id+"F5.wireOp",EDGE,"E318.bottom");var subQ2=makeQuery(id+"F5.imprint","INTERSECT",VERTEX,{"disambiguationData":[OD(0.0)],"derivedFrom":[subQ1,subQ0]});Q5=makeQuery(id+"F5.imprint","IMPRINT",FACE,{"disambiguationData":[TD([[makeQuery(id+"F5.imprint","IMPRINT",EDGE,{"disambiguationData":[TD([[subQ2,-1.0]])],"derivedFrom":subQ1}),-1.0]])]});}
            var Q6;
            {var subQ0=sQuery(id+"F5.wireOp",EDGE,"deff8420-59c7-402e-b318-feb89fa43c7f.0");var subQ1=sQuery(id+"F5.wireOp",EDGE,"E318.bottom");var subQ2=makeQuery(id+"F5.imprint","INTERSECT",VERTEX,{"disambiguationData":[OD(0.0)],"derivedFrom":[subQ1,subQ0]});Q6=makeQuery(id+"F5.imprint","IMPRINT",FACE,{"disambiguationData":[TD([[makeQuery(id+"F5.imprint","IMPRINT",EDGE,{"disambiguationData":[TD([[subQ2,-1.0]])],"derivedFrom":subQ1}),1.0]])]});}
            extrude(context, id + "F16", {"entities" : qUnion([Q0, Q1, Q2, Q3, Q4, Q5, Q6]), "operationType" : NewBodyOperationType.ADD, "depth" : 11 * mm, "offsetDistance" : 25 * mm});
        }
        {
            var Q0;
            Q0=makeQuery(id+"F6.imprint","IMPRINT",FACE,{"disambiguationData":[TD([[makeQuery(id+"F6.imprint","IMPRINT",EDGE,{"derivedFrom":sQuery(id+"F6.wireOp",EDGE,"E325")}),1.0]])]});
            var Q1;
            Q1=makeQuery(id+"F6.imprint","IMPRINT",FACE,{"disambiguationData":[TD([[makeQuery(id+"F6.imprint","IMPRINT",EDGE,{"derivedFrom":sQuery(id+"F6.wireOp",EDGE,"E336.0")}),1.0]])]});
            extrude(context, id + "F17", {"entities" : qUnion([Q0, Q1]), "operationType" : NewBodyOperationType.ADD, "depth" : 12 * mm, "offsetDistance" : 25 * mm});
        }
        {
            var Q0;
            Q0=makeQuery(id+"F6.imprint","IMPRINT",FACE,{"disambiguationData":[TD([[makeQuery(id+"F6.imprint","IMPRINT",EDGE,{"derivedFrom":sQuery(id+"F6.wireOp",EDGE,"E325")}),-1.0]])]});
            var Q1;
            Q1=makeQuery(id+"F6.imprint","IMPRINT",FACE,{"disambiguationData":[TD([[makeQuery(id+"F6.imprint","IMPRINT",EDGE,{"derivedFrom":sQuery(id+"F6.wireOp",EDGE,"E335")}),1.0]])]});
            extrude(context, id + "F18", {"entities" : qUnion([Q0, Q1]), "operationType" : NewBodyOperationType.ADD, "depth" : 13 * mm, "offsetDistance" : 25 * mm});
        }
        {
            var Q0;
            Q0=makeQuery(id+"F8.imprint","IMPRINT",FACE,{"disambiguationData":[TD([[makeQuery(id+"F8.imprint","IMPRINT",EDGE,{"derivedFrom":sQuery(id+"F8.wireOp",EDGE,"E419")}),1.0]])]});
            extrude(context, id + "F19", {"entities" : qUnion([Q0]), "operationType" : NewBodyOperationType.ADD, "depth" : 2 * mm, "offsetDistance" : 25 * mm});
        }
        {
            var Q0;
            Q0=makeQuery(id+"F8.imprint","IMPRINT",FACE,{"disambiguationData":[TD([[makeQuery(id+"F8.imprint","IMPRINT",EDGE,{"derivedFrom":sQuery(id+"F8.wireOp",EDGE,"E398.bottom")}),-1.0]])]});
            var Q1;
            Q1=makeQuery(id+"F8.imprint","IMPRINT",FACE,{"disambiguationData":[TD([[makeQuery(id+"F8.imprint","IMPRINT",EDGE,{"derivedFrom":sQuery(id+"F8.wireOp",EDGE,"E400.left")}),1.0]])]});
            var Q2;
            Q2=makeQuery(id+"F8.imprint","IMPRINT",FACE,{"disambiguationData":[TD([[makeQuery(id+"F8.imprint","IMPRINT",EDGE,{"derivedFrom":sQuery(id+"F8.wireOp",EDGE,"E382")}),1.0]])]});
            var Q3;
            Q3=makeQuery(id+"F8.imprint","IMPRINT",FACE,{"disambiguationData":[TD([[makeQuery(id+"F8.imprint","IMPRINT",EDGE,{"derivedFrom":sQuery(id+"F8.wireOp",EDGE,"E390")}),1.0]])]});
            var Q4;
            Q4=makeQuery(id+"F8.imprint","IMPRINT",FACE,{"disambiguationData":[TD([[makeQuery(id+"F8.imprint","IMPRINT",EDGE,{"derivedFrom":sQuery(id+"F8.wireOp",EDGE,"E375.bottom")}),-1.0]])]});
            var Q5;
            Q5=makeQuery(id+"F8.imprint","IMPRINT",FACE,{"disambiguationData":[TD([[makeQuery(id+"F8.imprint","IMPRINT",EDGE,{"derivedFrom":sQuery(id+"F8.wireOp",EDGE,"E374.bottom")}),-1.0]])]});
            var Q6;
            Q6=makeQuery(id+"F8.imprint","IMPRINT",FACE,{"disambiguationData":[TD([[makeQuery(id+"F8.imprint","IMPRINT",EDGE,{"derivedFrom":sQuery(id+"F8.wireOp",EDGE,"E366")}),1.0]])]});
            var Q7;
            Q7=makeQuery(id+"F8.imprint","IMPRINT",FACE,{"disambiguationData":[TD([[makeQuery(id+"F8.imprint","IMPRINT",EDGE,{"derivedFrom":sQuery(id+"F8.wireOp",EDGE,"E362")}),-1.0]])]});
            var Q8;
            Q8=makeQuery(id+"F8.imprint","IMPRINT",FACE,{"disambiguationData":[TD([[makeQuery(id+"F8.imprint","IMPRINT",EDGE,{"derivedFrom":sQuery(id+"F8.wireOp",EDGE,"E347")}),1.0]])]});
            var Q9;
            Q9=makeQuery(id+"F8.imprint","IMPRINT",FACE,{"disambiguationData":[TD([[makeQuery(id+"F8.imprint","IMPRINT",EDGE,{"derivedFrom":sQuery(id+"F8.wireOp",EDGE,"E344.bottom")}),-1.0]])]});
            extrude(context, id + "F20", {"entities" : qUnion([Q0, Q1, Q2, Q3, Q4, Q5, Q6, Q7, Q8, Q9]), "operationType" : NewBodyOperationType.ADD, "depth" : 1 * mm, "offsetDistance" : 25 * mm});
        }
    });
